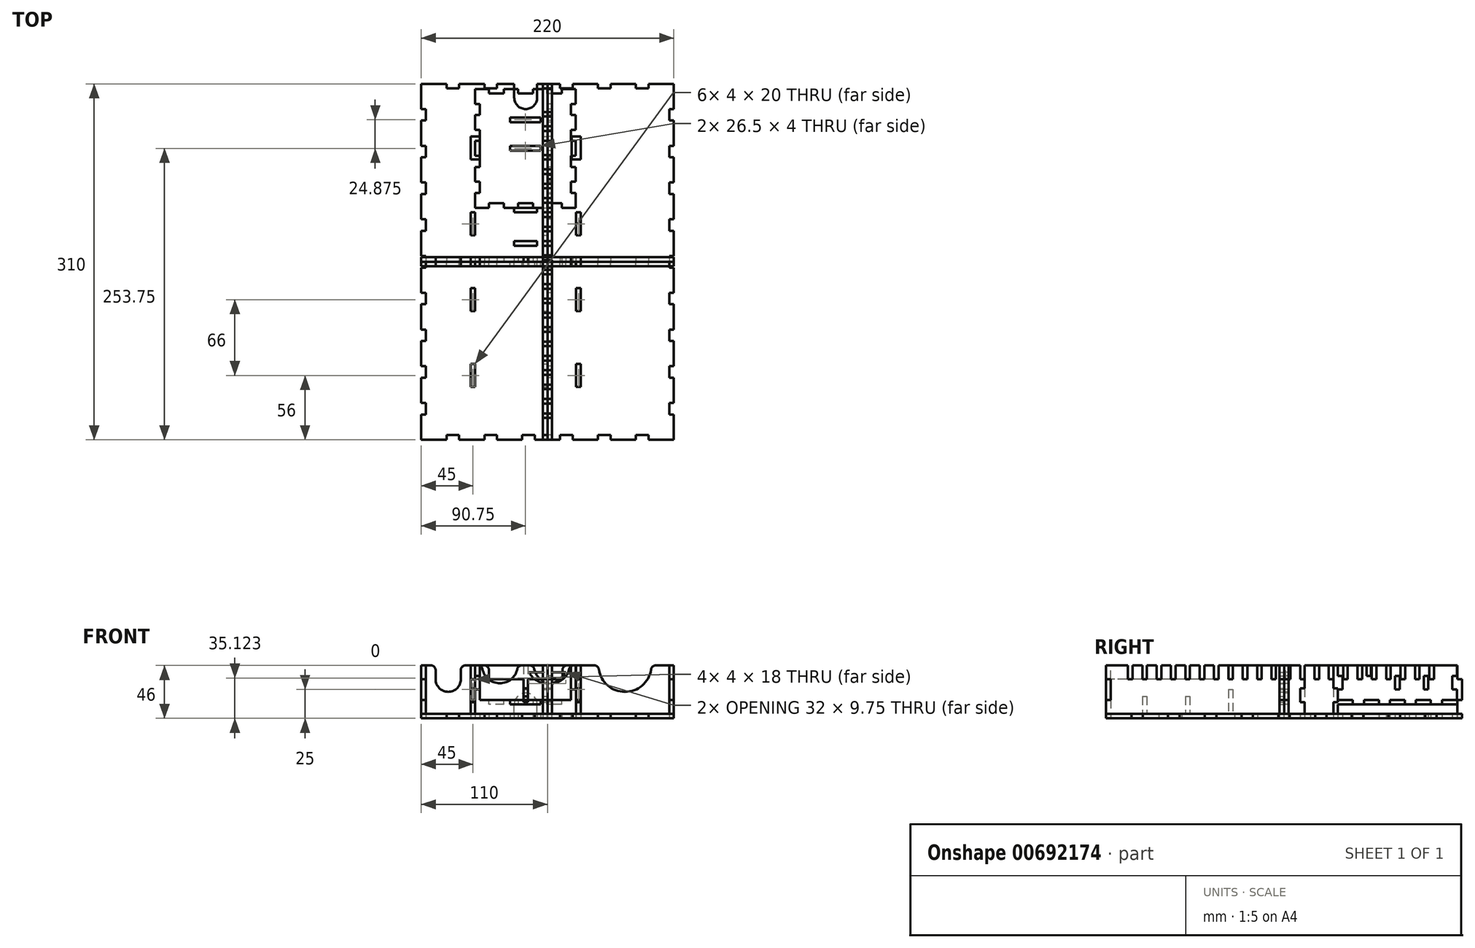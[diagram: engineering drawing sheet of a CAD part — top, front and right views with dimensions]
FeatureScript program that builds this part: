
annotation { "Feature Type Name" : "Feature", "Feature Type Description" : "" }
export const myFeature = defineFeature(function(context is Context, id is Id, definition is map)
    precondition{}
    {
        {
            assignVariable(context, id + "F0", {"name" : "thickness", "anyValue" : 4});
        }
        {
            var Q0;
            Q0=qCreatedBy(makeId("Top.planeOp"),FACE);
            var sketch = newSketch(context, id + "F1", { "sketchPlane" : qUnion([Q0])});
            skLineSegment(sketch, "E0", {"start": v(-110, 155) * mm, "end": v(-110, 133) * mm});
            skLineSegment(sketch, "E1", {"start": v(-110, 133) * mm, "end": v(-106, 133) * mm});
            skLineSegment(sketch, "E2", {"start": v(-106, 133) * mm, "end": v(-106, 123) * mm});
            skLineSegment(sketch, "E3", {"start": v(-106, 123) * mm, "end": v(-110, 123) * mm});
            skLineSegment(sketch, "E4.0.1.0", {"start": v(-106, 91) * mm, "end": v(-110, 91) * mm});
            skLineSegment(sketch, "E4.0.1.1", {"start": v(-110, 123) * mm, "end": v(-110, 101) * mm});
            skLineSegment(sketch, "E4.0.1.2", {"start": v(-106, 101) * mm, "end": v(-106, 91) * mm});
            skLineSegment(sketch, "E4.0.1.3", {"start": v(-110, 101) * mm, "end": v(-106, 101) * mm});
            skLineSegment(sketch, "E4.0.2.0", {"start": v(-106, 59) * mm, "end": v(-110, 59) * mm});
            skLineSegment(sketch, "E4.0.2.1", {"start": v(-110, 91) * mm, "end": v(-110, 69) * mm});
            skLineSegment(sketch, "E4.0.2.2", {"start": v(-106, 69) * mm, "end": v(-106, 59) * mm});
            skLineSegment(sketch, "E4.0.2.3", {"start": v(-110, 69) * mm, "end": v(-106, 69) * mm});
            skLineSegment(sketch, "E4.0.3.0", {"start": v(-106, 27) * mm, "end": v(-110, 27) * mm});
            skLineSegment(sketch, "E4.0.3.1", {"start": v(-110, 59) * mm, "end": v(-110, 37) * mm});
            skLineSegment(sketch, "E4.0.3.2", {"start": v(-106, 37) * mm, "end": v(-106, 27) * mm});
            skLineSegment(sketch, "E4.0.3.3", {"start": v(-110, 37) * mm, "end": v(-106, 37) * mm});
            skLineSegment(sketch, "E4.0.4.0", {"start": v(-106, -5) * mm, "end": v(-110, -5) * mm});
            skLineSegment(sketch, "E4.0.4.1", {"start": v(-110, 27) * mm, "end": v(-110, 5) * mm});
            skLineSegment(sketch, "E4.0.4.2", {"start": v(-106, 5) * mm, "end": v(-106, -5) * mm});
            skLineSegment(sketch, "E4.0.4.3", {"start": v(-110, 5) * mm, "end": v(-106, 5) * mm});
            skLineSegment(sketch, "E4.0.5.0", {"start": v(-106, -37) * mm, "end": v(-110, -37) * mm});
            skLineSegment(sketch, "E4.0.5.1", {"start": v(-110, -5) * mm, "end": v(-110, -27) * mm});
            skLineSegment(sketch, "E4.0.5.2", {"start": v(-106, -27) * mm, "end": v(-106, -37) * mm});
            skLineSegment(sketch, "E4.0.5.3", {"start": v(-110, -27) * mm, "end": v(-106, -27) * mm});
            skLineSegment(sketch, "E4.0.6.0", {"start": v(-106, -69) * mm, "end": v(-110, -69) * mm});
            skLineSegment(sketch, "E4.0.6.1", {"start": v(-110, -37) * mm, "end": v(-110, -59) * mm});
            skLineSegment(sketch, "E4.0.6.2", {"start": v(-106, -59) * mm, "end": v(-106, -69) * mm});
            skLineSegment(sketch, "E4.0.6.3", {"start": v(-110, -59) * mm, "end": v(-106, -59) * mm});
            skLineSegment(sketch, "E4.0.7.0", {"start": v(-106, -101) * mm, "end": v(-110, -101) * mm});
            skLineSegment(sketch, "E4.0.7.1", {"start": v(-110, -69) * mm, "end": v(-110, -91) * mm});
            skLineSegment(sketch, "E4.0.7.2", {"start": v(-106, -91) * mm, "end": v(-106, -101) * mm});
            skLineSegment(sketch, "E4.0.7.3", {"start": v(-110, -91) * mm, "end": v(-106, -91) * mm});
            skLineSegment(sketch, "E4.0.8.0", {"start": v(-106, -133) * mm, "end": v(-110, -133) * mm});
            skLineSegment(sketch, "E4.0.8.1", {"start": v(-110, -101) * mm, "end": v(-110, -123) * mm});
            skLineSegment(sketch, "E4.0.8.2", {"start": v(-106, -123) * mm, "end": v(-106, -133) * mm});
            skLineSegment(sketch, "E4.0.8.3", {"start": v(-110, -123) * mm, "end": v(-106, -123) * mm});
            skLineSegment(sketch, "E4.0.9.1", {"start": v(-110, -133) * mm, "end": v(-110, -155) * mm});
            skLineSegment(sketch, "E5", {"start": v(-110, 155) * mm, "end": v(-88, 155) * mm});
            skLineSegment(sketch, "E6", {"start": v(-88, 155) * mm, "end": v(-88, 151) * mm});
            skLineSegment(sketch, "E7", {"start": v(-88, 151) * mm, "end": v(-77, 151) * mm});
            skLineSegment(sketch, "E8", {"start": v(-77, 151) * mm, "end": v(-77, 155) * mm});
            skLineSegment(sketch, "E9.1.0.0", {"start": v(-44, 151) * mm, "end": v(-44, 155) * mm});
            skLineSegment(sketch, "E9.1.0.1", {"start": v(-55, 151) * mm, "end": v(-44, 151) * mm});
            skLineSegment(sketch, "E9.1.0.2", {"start": v(-77, 155) * mm, "end": v(-55, 155) * mm});
            skLineSegment(sketch, "E9.1.0.3", {"start": v(-55, 155) * mm, "end": v(-55, 151) * mm});
            skLineSegment(sketch, "E9.2.0.0", {"start": v(-11, 151) * mm, "end": v(-11, 155) * mm, "construction": true});
            skLineSegment(sketch, "E9.2.0.1", {"start": v(-22, 151) * mm, "end": v(-11, 151) * mm, "construction": true});
            skLineSegment(sketch, "E9.2.0.2", {"start": v(-44, 155) * mm, "end": v(-22, 155) * mm, "construction": true});
            skLineSegment(sketch, "E9.2.0.3", {"start": v(-22, 155) * mm, "end": v(-22, 151) * mm, "construction": true});
            skLineSegment(sketch, "E9.3.0.0", {"start": v(22, 151) * mm, "end": v(22, 155) * mm});
            skLineSegment(sketch, "E9.3.0.1", {"start": v(11, 151) * mm, "end": v(22, 151) * mm});
            skLineSegment(sketch, "E9.3.0.2", {"start": v(-11, 155) * mm, "end": v(11, 155) * mm, "construction": true});
            skLineSegment(sketch, "E9.3.0.3", {"start": v(11, 155) * mm, "end": v(11, 151) * mm});
            skLineSegment(sketch, "E9.4.0.0", {"start": v(55, 151) * mm, "end": v(55, 155) * mm});
            skLineSegment(sketch, "E9.4.0.1", {"start": v(44, 151) * mm, "end": v(55, 151) * mm});
            skLineSegment(sketch, "E9.4.0.2", {"start": v(22, 155) * mm, "end": v(44, 155) * mm});
            skLineSegment(sketch, "E9.4.0.3", {"start": v(44, 155) * mm, "end": v(44, 151) * mm});
            skLineSegment(sketch, "E9.5.0.0", {"start": v(88, 151) * mm, "end": v(88, 155) * mm});
            skLineSegment(sketch, "E9.5.0.1", {"start": v(77, 151) * mm, "end": v(88, 151) * mm});
            skLineSegment(sketch, "E9.5.0.2", {"start": v(55, 155) * mm, "end": v(77, 155) * mm});
            skLineSegment(sketch, "E9.5.0.3", {"start": v(77, 155) * mm, "end": v(77, 151) * mm});
            skLineSegment(sketch, "E9.6.0.2", {"start": v(88, 155) * mm, "end": v(110, 155) * mm});
            skPoint(sketch, "E10.endSnap0", {"position": v(-106, 0) * mm});
            skLineSegment(sketch, "E11.MirrorCS", {"start": v(106, -37) * mm, "end": v(110, -37) * mm});
            skLineSegment(sketch, "E12.MirrorCS", {"start": v(106, -27) * mm, "end": v(106, -37) * mm});
            skLineSegment(sketch, "E13.MirrorCS", {"start": v(106, -5) * mm, "end": v(110, -5) * mm});
            skLineSegment(sketch, "E14.MirrorCS", {"start": v(110, -133) * mm, "end": v(110, -155) * mm});
            skLineSegment(sketch, "E15.MirrorCS", {"start": v(106, 133) * mm, "end": v(106, 123) * mm});
            skLineSegment(sketch, "E16.MirrorCS", {"start": v(110, -59) * mm, "end": v(106, -59) * mm});
            skLineSegment(sketch, "E17.MirrorCS", {"start": v(110, -123) * mm, "end": v(106, -123) * mm});
            skLineSegment(sketch, "E18.MirrorCS", {"start": v(106, -91) * mm, "end": v(106, -101) * mm});
            skLineSegment(sketch, "E19.MirrorCS", {"start": v(106, -133) * mm, "end": v(110, -133) * mm});
            skLineSegment(sketch, "E20.MirrorCS", {"start": v(110, 69) * mm, "end": v(106, 69) * mm});
            skLineSegment(sketch, "E21.MirrorCS", {"start": v(106, 27) * mm, "end": v(110, 27) * mm});
            skLineSegment(sketch, "E22.MirrorCS", {"start": v(106, -101) * mm, "end": v(110, -101) * mm});
            skLineSegment(sketch, "E23.MirrorCS", {"start": v(110, -5) * mm, "end": v(110, -27) * mm});
            skLineSegment(sketch, "E24.MirrorCS", {"start": v(106, -59) * mm, "end": v(106, -69) * mm});
            skLineSegment(sketch, "E25.MirrorCS", {"start": v(106, 37) * mm, "end": v(106, 27) * mm});
            skLineSegment(sketch, "E26.MirrorCS", {"start": v(110, 133) * mm, "end": v(106, 133) * mm});
            skLineSegment(sketch, "E27.MirrorCS", {"start": v(106, 69) * mm, "end": v(106, 59) * mm});
            skLineSegment(sketch, "E28.MirrorCS", {"start": v(106, 59) * mm, "end": v(110, 59) * mm});
            skLineSegment(sketch, "E29.MirrorCS", {"start": v(110, 37) * mm, "end": v(106, 37) * mm});
            skLineSegment(sketch, "E30.MirrorCS", {"start": v(106, -69) * mm, "end": v(110, -69) * mm});
            skLineSegment(sketch, "E31.MirrorCS", {"start": v(106, 91) * mm, "end": v(110, 91) * mm});
            skLineSegment(sketch, "E32.MirrorCS", {"start": v(106, 101) * mm, "end": v(106, 91) * mm});
            skLineSegment(sketch, "E33.MirrorCS", {"start": v(110, 27) * mm, "end": v(110, 5) * mm});
            skLineSegment(sketch, "E34.MirrorCS", {"start": v(110, 5) * mm, "end": v(106, 5) * mm});
            skLineSegment(sketch, "E35.MirrorCS", {"start": v(110, 155) * mm, "end": v(110, 133) * mm});
            skLineSegment(sketch, "E36.MirrorCS", {"start": v(110, -101) * mm, "end": v(110, -123) * mm});
            skLineSegment(sketch, "E37.MirrorCS", {"start": v(106, 123) * mm, "end": v(110, 123) * mm});
            skLineSegment(sketch, "E38.MirrorCS", {"start": v(110, -27) * mm, "end": v(106, -27) * mm});
            skLineSegment(sketch, "E39.MirrorCS", {"start": v(106, -123) * mm, "end": v(106, -133) * mm});
            skLineSegment(sketch, "E40.MirrorCS", {"start": v(110, -91) * mm, "end": v(106, -91) * mm});
            skLineSegment(sketch, "E41.MirrorCS", {"start": v(106, 5) * mm, "end": v(106, -5) * mm});
            skLineSegment(sketch, "E42.MirrorCS", {"start": v(110, 101) * mm, "end": v(106, 101) * mm});
            skLineSegment(sketch, "E43.MirrorCS", {"start": v(110, 59) * mm, "end": v(110, 37) * mm});
            skLineSegment(sketch, "E44.MirrorCS", {"start": v(110, -69) * mm, "end": v(110, -91) * mm});
            skLineSegment(sketch, "E45.MirrorCS", {"start": v(110, 91) * mm, "end": v(110, 69) * mm});
            skLineSegment(sketch, "E46.MirrorCS", {"start": v(110, -37) * mm, "end": v(110, -59) * mm});
            skLineSegment(sketch, "E47.MirrorCS", {"start": v(110, 123) * mm, "end": v(110, 101) * mm});
            skLineSegment(sketch, "E48.MirrorCS", {"start": v(-11, -151) * mm, "end": v(-11, -155) * mm});
            skLineSegment(sketch, "E49.MirrorCS", {"start": v(22, -155) * mm, "end": v(44, -155) * mm});
            skLineSegment(sketch, "E50.MirrorCS", {"start": v(-55, -151) * mm, "end": v(-44, -151) * mm});
            skLineSegment(sketch, "E51.MirrorCS", {"start": v(-44, -151) * mm, "end": v(-44, -155) * mm});
            skLineSegment(sketch, "E52.MirrorCS", {"start": v(11, -151) * mm, "end": v(22, -151) * mm});
            skLineSegment(sketch, "E53.MirrorCS", {"start": v(22, -151) * mm, "end": v(22, -155) * mm});
            skLineSegment(sketch, "E54.MirrorCS", {"start": v(-22, -151) * mm, "end": v(-11, -151) * mm});
            skLineSegment(sketch, "E55.MirrorCS", {"start": v(77, -151) * mm, "end": v(88, -151) * mm});
            skLineSegment(sketch, "E56.MirrorCS", {"start": v(-11, -155) * mm, "end": v(11, -155) * mm});
            skLineSegment(sketch, "E57.MirrorCS", {"start": v(-77, -155) * mm, "end": v(-55, -155) * mm});
            skLineSegment(sketch, "E58.MirrorCS", {"start": v(-88, -155) * mm, "end": v(-88, -151) * mm});
            skLineSegment(sketch, "E59.MirrorCS", {"start": v(-22, -155) * mm, "end": v(-22, -151) * mm});
            skLineSegment(sketch, "E60.MirrorCS", {"start": v(44, -155) * mm, "end": v(44, -151) * mm});
            skLineSegment(sketch, "E61.MirrorCS", {"start": v(44, -151) * mm, "end": v(55, -151) * mm});
            skLineSegment(sketch, "E62.MirrorCS", {"start": v(-77, -151) * mm, "end": v(-77, -155) * mm});
            skLineSegment(sketch, "E63.MirrorCS", {"start": v(77, -155) * mm, "end": v(77, -151) * mm});
            skLineSegment(sketch, "E64.MirrorCS", {"start": v(88, -155) * mm, "end": v(110, -155) * mm});
            skLineSegment(sketch, "E65.MirrorCS", {"start": v(-110, -155) * mm, "end": v(-88, -155) * mm});
            skLineSegment(sketch, "E66.MirrorCS", {"start": v(11, -155) * mm, "end": v(11, -151) * mm});
            skLineSegment(sketch, "E67.MirrorCS", {"start": v(-55, -155) * mm, "end": v(-55, -151) * mm});
            skLineSegment(sketch, "E68.MirrorCS", {"start": v(55, -151) * mm, "end": v(55, -155) * mm});
            skLineSegment(sketch, "E69.MirrorCS", {"start": v(88, -151) * mm, "end": v(88, -155) * mm});
            skLineSegment(sketch, "E70.MirrorCS", {"start": v(-88, -151) * mm, "end": v(-77, -151) * mm});
            skLineSegment(sketch, "E71.MirrorCS", {"start": v(55, -155) * mm, "end": v(77, -155) * mm});
            skLineSegment(sketch, "E72.MirrorCS", {"start": v(-44, -155) * mm, "end": v(-22, -155) * mm});
            skLineSegment(sketch, "E73", {"start": v(-65, 163.65) * mm, "end": v(-65, -222.9) * mm, "construction": true});
            skLineSegment(sketch, "E74", {"start": v(-19, 166.4) * mm, "end": v(-19, -214.65) * mm, "construction": true});
            skLineSegment(sketch, "E75", {"start": v(27, 161.08) * mm, "end": v(27, -222.02) * mm, "construction": true});
            skLineSegment(sketch, "E76", {"start": v(-29, 155) * mm, "end": v(-29, 143) * mm});
            skLineSegment(sketch, "E77", {"start": v(-9, 155) * mm, "end": v(-9, 143) * mm});
            skArc(sketch, "E78", {"start": v(-29, 143) * mm, "mid": v(-19, 133) * mm, "end": v(-9, 143) * mm});
            skLineSegment(sketch, "E79", {"start": v(-44, 155) * mm, "end": v(-29, 155) * mm});
            skLineSegment(sketch, "E80", {"start": v(-9, 155) * mm, "end": v(11, 155) * mm});
            skLineSegment(sketch, "E81.bottom", {"start": v(21, 109) * mm, "end": v(29, 109) * mm});
            skLineSegment(sketch, "E81.top", {"start": v(21, 89) * mm, "end": v(29, 89) * mm});
            skLineSegment(sketch, "E81.left", {"start": v(21, 109) * mm, "end": v(21, 89) * mm});
            skLineSegment(sketch, "E81.right", {"start": v(29, 109) * mm, "end": v(29, 89) * mm});
            skLineSegment(sketch, "E82.bottom", {"start": v(25, 43) * mm, "end": v(29, 43) * mm});
            skLineSegment(sketch, "E82.top", {"start": v(25, 23) * mm, "end": v(29, 23) * mm});
            skLineSegment(sketch, "E82.left", {"start": v(25, 43) * mm, "end": v(25, 23) * mm});
            skLineSegment(sketch, "E82.right", {"start": v(29, 43) * mm, "end": v(29, 23) * mm});
            skLineSegment(sketch, "E83.bottom", {"start": v(25, -23) * mm, "end": v(29, -23) * mm});
            skLineSegment(sketch, "E83.top", {"start": v(25, -43) * mm, "end": v(29, -43) * mm});
            skLineSegment(sketch, "E83.left", {"start": v(25, -23) * mm, "end": v(25, -43) * mm});
            skLineSegment(sketch, "E83.right", {"start": v(29, -23) * mm, "end": v(29, -43) * mm});
            skLineSegment(sketch, "E84.bottom", {"start": v(25, -89) * mm, "end": v(29, -89) * mm});
            skLineSegment(sketch, "E84.top", {"start": v(25, -109) * mm, "end": v(29, -109) * mm});
            skLineSegment(sketch, "E84.left", {"start": v(25, -89) * mm, "end": v(25, -109) * mm});
            skLineSegment(sketch, "E84.right", {"start": v(29, -89) * mm, "end": v(29, -109) * mm});
            skLineSegment(sketch, "E85", {"start": v(29, 109) * mm, "end": v(29, 155) * mm, "construction": true});
            skPoint(sketch, "E85.endSnap0", {"position": v(33, 155) * mm});
            skLineSegment(sketch, "E86", {"start": v(29, 89) * mm, "end": v(29, 43) * mm, "construction": true});
            skLineSegment(sketch, "E87", {"start": v(29, 23) * mm, "end": v(29, -23) * mm, "construction": true});
            skLineSegment(sketch, "E88", {"start": v(29, -43) * mm, "end": v(29, -89) * mm, "construction": true});
            skLineSegment(sketch, "E89", {"start": v(29, -109) * mm, "end": v(29, -155) * mm, "construction": true});
            skLineSegment(sketch, "E90.MirrorCS", {"start": v(-63, -109) * mm, "end": v(-67, -109) * mm});
            skLineSegment(sketch, "E91.MirrorCS", {"start": v(-59, 109) * mm, "end": v(-67, 109) * mm});
            skLineSegment(sketch, "E92.MirrorCS", {"start": v(-63, 43) * mm, "end": v(-67, 43) * mm});
            skLineSegment(sketch, "E93.MirrorCS", {"start": v(-59, 89) * mm, "end": v(-67, 89) * mm});
            skLineSegment(sketch, "E94.MirrorCS", {"start": v(-63, -23) * mm, "end": v(-67, -23) * mm});
            skLineSegment(sketch, "E95.MirrorCS", {"start": v(-63, 23) * mm, "end": v(-67, 23) * mm});
            skLineSegment(sketch, "E96.MirrorCS", {"start": v(-63, -89) * mm, "end": v(-67, -89) * mm});
            skLineSegment(sketch, "E97.MirrorCS", {"start": v(-63, -43) * mm, "end": v(-67, -43) * mm});
            skLineSegment(sketch, "E98.MirrorCS", {"start": v(-67, -89) * mm, "end": v(-67, -109) * mm});
            skLineSegment(sketch, "E99.MirrorCS", {"start": v(-67, -23) * mm, "end": v(-67, -43) * mm});
            skLineSegment(sketch, "E100.MirrorCS", {"start": v(-59, 109) * mm, "end": v(-59, 89) * mm});
            skLineSegment(sketch, "E101.MirrorCS", {"start": v(-63, 43) * mm, "end": v(-63, 23) * mm});
            skLineSegment(sketch, "E102.MirrorCS", {"start": v(-67, 109) * mm, "end": v(-67, 89) * mm});
            skLineSegment(sketch, "E103.MirrorCS", {"start": v(-67, 43) * mm, "end": v(-67, 23) * mm});
            skLineSegment(sketch, "E104.MirrorCS", {"start": v(-63, -89) * mm, "end": v(-63, -109) * mm});
            skLineSegment(sketch, "E105.MirrorCS", {"start": v(-63, -23) * mm, "end": v(-63, -43) * mm});
            skLineSegment(sketch, "E106", {"start": v(-151.25, 45) * mm, "end": v(136.26, 45) * mm, "construction": true});
            skLineSegment(sketch, "E107", {"start": v(137.08, 16) * mm, "end": v(-152.07, 16) * mm, "construction": true});
            skLineSegment(sketch, "E108.bottom", {"start": v(-29, 47) * mm, "end": v(-9, 47) * mm});
            skLineSegment(sketch, "E108.top", {"start": v(-29, 43) * mm, "end": v(-9, 43) * mm});
            skLineSegment(sketch, "E108.left", {"start": v(-29, 47) * mm, "end": v(-29, 43) * mm});
            skLineSegment(sketch, "E108.right", {"start": v(-9, 47) * mm, "end": v(-9, 43) * mm});
            skLineSegment(sketch, "E109.bottom", {"start": v(-29, 18) * mm, "end": v(-9, 18) * mm});
            skLineSegment(sketch, "E109.top", {"start": v(-29, 14) * mm, "end": v(-9, 14) * mm});
            skLineSegment(sketch, "E109.left", {"start": v(-29, 18) * mm, "end": v(-29, 14) * mm});
            skLineSegment(sketch, "E109.right", {"start": v(-9, 18) * mm, "end": v(-9, 14) * mm});
            skSolve(sketch);
        }
        {
            var Q0;
            Q0=qSketchRegion(id+"F1",true);
            extrude(context, id + "F2", {"entities" : qUnion([Q0]), "depth" : 4 * mm});
        }
        {
            var Q0;
            Q0=qCreatedBy(makeId("Right.planeOp"),FACE);
            var sketch = newSketch(context, id + "F3", { "sketchPlane" : qUnion([Q0])});
            skLineSegment(sketch, "E110.top", {"start": v(-151, 4) * mm, "end": v(151, 4) * mm});
            skLineSegment(sketch, "E111.bottom", {"start": v(-151, 34) * mm, "end": v(-155, 34) * mm});
            skLineSegment(sketch, "E111.top", {"start": v(-151, 16) * mm, "end": v(-155, 16) * mm});
            skPoint(sketch, "E112.oppositeSnap0", {"position": v(-153, 16) * mm});
            skLineSegment(sketch, "E112.bottom", {"start": v(155, 34) * mm, "end": v(151, 34) * mm});
            skLineSegment(sketch, "E112.top", {"start": v(155, 16) * mm, "end": v(151, 16) * mm});
            skLineSegment(sketch, "E113.bottom", {"start": v(-133, 0) * mm, "end": v(-123, 0) * mm});
            skLineSegment(sketch, "E113.top", {"start": v(-133, 4) * mm, "end": v(-123, 4) * mm});
            skLineSegment(sketch, "E113.left", {"start": v(-133, 0) * mm, "end": v(-133, 4) * mm});
            skLineSegment(sketch, "E113.right", {"start": v(-123, 0) * mm, "end": v(-123, 4) * mm});
            skLineSegment(sketch, "E114.1.0.0", {"start": v(-101, 4) * mm, "end": v(-91, 4) * mm});
            skLineSegment(sketch, "E114.1.0.1", {"start": v(-101, 0) * mm, "end": v(-101, 4) * mm});
            skLineSegment(sketch, "E114.1.0.2", {"start": v(-91, 0) * mm, "end": v(-91, 4) * mm});
            skLineSegment(sketch, "E114.1.0.3", {"start": v(-101, 0) * mm, "end": v(-91, 0) * mm});
            skLineSegment(sketch, "E114.2.0.0", {"start": v(-69, 4) * mm, "end": v(-59, 4) * mm});
            skLineSegment(sketch, "E114.2.0.1", {"start": v(-69, 0) * mm, "end": v(-69, 4) * mm});
            skLineSegment(sketch, "E114.2.0.2", {"start": v(-59, 0) * mm, "end": v(-59, 4) * mm});
            skLineSegment(sketch, "E114.2.0.3", {"start": v(-69, 0) * mm, "end": v(-59, 0) * mm});
            skLineSegment(sketch, "E114.3.0.0", {"start": v(-37, 4) * mm, "end": v(-27, 4) * mm});
            skLineSegment(sketch, "E114.3.0.1", {"start": v(-37, 0) * mm, "end": v(-37, 4) * mm});
            skLineSegment(sketch, "E114.3.0.2", {"start": v(-27, 0) * mm, "end": v(-27, 4) * mm});
            skLineSegment(sketch, "E114.3.0.3", {"start": v(-37, 0) * mm, "end": v(-27, 0) * mm});
            skLineSegment(sketch, "E114.4.0.0", {"start": v(-5, 4) * mm, "end": v(5, 4) * mm});
            skLineSegment(sketch, "E114.4.0.1", {"start": v(-5, 0) * mm, "end": v(-5, 4) * mm});
            skLineSegment(sketch, "E114.4.0.2", {"start": v(5, 0) * mm, "end": v(5, 4) * mm});
            skLineSegment(sketch, "E114.4.0.3", {"start": v(-5, 0) * mm, "end": v(5, 0) * mm});
            skLineSegment(sketch, "E114.5.0.0", {"start": v(27, 4) * mm, "end": v(37, 4) * mm});
            skLineSegment(sketch, "E114.5.0.1", {"start": v(27, 0) * mm, "end": v(27, 4) * mm});
            skLineSegment(sketch, "E114.5.0.2", {"start": v(37, 0) * mm, "end": v(37, 4) * mm});
            skLineSegment(sketch, "E114.5.0.3", {"start": v(27, 0) * mm, "end": v(37, 0) * mm});
            skLineSegment(sketch, "E114.6.0.0", {"start": v(59, 4) * mm, "end": v(69, 4) * mm});
            skLineSegment(sketch, "E114.6.0.1", {"start": v(59, 0) * mm, "end": v(59, 4) * mm});
            skLineSegment(sketch, "E114.6.0.2", {"start": v(69, 0) * mm, "end": v(69, 4) * mm});
            skLineSegment(sketch, "E114.6.0.3", {"start": v(59, 0) * mm, "end": v(69, 0) * mm});
            skLineSegment(sketch, "E114.7.0.0", {"start": v(91, 4) * mm, "end": v(101, 4) * mm});
            skLineSegment(sketch, "E114.7.0.1", {"start": v(91, 0) * mm, "end": v(91, 4) * mm});
            skLineSegment(sketch, "E114.7.0.2", {"start": v(101, 0) * mm, "end": v(101, 4) * mm});
            skLineSegment(sketch, "E114.7.0.3", {"start": v(91, 0) * mm, "end": v(101, 0) * mm});
            skLineSegment(sketch, "E114.8.0.0", {"start": v(123, 4) * mm, "end": v(133, 4) * mm});
            skLineSegment(sketch, "E114.8.0.1", {"start": v(123, 0) * mm, "end": v(123, 4) * mm});
            skLineSegment(sketch, "E114.8.0.2", {"start": v(133, 0) * mm, "end": v(133, 4) * mm});
            skLineSegment(sketch, "E114.8.0.3", {"start": v(123, 0) * mm, "end": v(133, 0) * mm});
            skLineSegment(sketch, "E114.direction1", {"start": v(-133, 0) * mm, "end": v(-101, 0) * mm, "construction": true});
            skLineSegment(sketch, "E115.top", {"start": v(-151, 46) * mm, "end": v(-136, 46) * mm});
            skLineSegment(sketch, "E115.right", {"start": v(-136, 34) * mm, "end": v(-136, 46) * mm});
            skLineSegment(sketch, "E116.top", {"start": v(151, 46) * mm, "end": v(130.5, 46) * mm});
            skLineSegment(sketch, "E116.right", {"start": v(130.5, 34) * mm, "end": v(130.5, 46) * mm});
            skLineSegment(sketch, "E117.top", {"start": v(-132, 46) * mm, "end": v(-123.5, 46) * mm});
            skLineSegment(sketch, "E117.left", {"start": v(-132, 34) * mm, "end": v(-132, 46) * mm});
            skLineSegment(sketch, "E117.right", {"start": v(-123.5, 34) * mm, "end": v(-123.5, 46) * mm});
            skLineSegment(sketch, "E118", {"start": v(-136, 34) * mm, "end": v(-132, 34) * mm});
            skLineSegment(sketch, "E119", {"start": v(130.5, 34) * mm, "end": v(126.5, 34) * mm});
            skLineSegment(sketch, "E120.1.0.0", {"start": v(-123.5, 34) * mm, "end": v(-119.5, 34) * mm});
            skLineSegment(sketch, "E120.1.0.1", {"start": v(-111, 34) * mm, "end": v(-111, 46) * mm});
            skLineSegment(sketch, "E120.1.0.2", {"start": v(-119.5, 46) * mm, "end": v(-111, 46) * mm});
            skLineSegment(sketch, "E120.1.0.3", {"start": v(-119.5, 34) * mm, "end": v(-119.5, 46) * mm});
            skLineSegment(sketch, "E120.2.0.0", {"start": v(-111, 34) * mm, "end": v(-107, 34) * mm});
            skLineSegment(sketch, "E120.2.0.1", {"start": v(-98.5, 34) * mm, "end": v(-98.5, 46) * mm});
            skLineSegment(sketch, "E120.2.0.2", {"start": v(-107, 46) * mm, "end": v(-98.5, 46) * mm});
            skLineSegment(sketch, "E120.2.0.3", {"start": v(-107, 34) * mm, "end": v(-107, 46) * mm});
            skLineSegment(sketch, "E120.3.0.0", {"start": v(-98.5, 34) * mm, "end": v(-94.5, 34) * mm});
            skLineSegment(sketch, "E120.3.0.1", {"start": v(-86, 34) * mm, "end": v(-86, 46) * mm});
            skLineSegment(sketch, "E120.3.0.2", {"start": v(-94.5, 46) * mm, "end": v(-86, 46) * mm});
            skLineSegment(sketch, "E120.3.0.3", {"start": v(-94.5, 34) * mm, "end": v(-94.5, 46) * mm});
            skLineSegment(sketch, "E120.4.0.0", {"start": v(-86, 34) * mm, "end": v(-82, 34) * mm});
            skLineSegment(sketch, "E120.4.0.1", {"start": v(-73.5, 34) * mm, "end": v(-73.5, 46) * mm});
            skLineSegment(sketch, "E120.4.0.2", {"start": v(-82, 46) * mm, "end": v(-73.5, 46) * mm});
            skLineSegment(sketch, "E120.4.0.3", {"start": v(-82, 34) * mm, "end": v(-82, 46) * mm});
            skLineSegment(sketch, "E120.5.0.0", {"start": v(-73.5, 34) * mm, "end": v(-69.5, 34) * mm});
            skLineSegment(sketch, "E120.5.0.1", {"start": v(-61, 34) * mm, "end": v(-61, 46) * mm});
            skLineSegment(sketch, "E120.5.0.2", {"start": v(-69.5, 46) * mm, "end": v(-61, 46) * mm});
            skLineSegment(sketch, "E120.5.0.3", {"start": v(-69.5, 34) * mm, "end": v(-69.5, 46) * mm});
            skLineSegment(sketch, "E120.6.0.0", {"start": v(-61, 34) * mm, "end": v(-57, 34) * mm});
            skLineSegment(sketch, "E120.6.0.1", {"start": v(-48.5, 34) * mm, "end": v(-48.5, 46) * mm});
            skLineSegment(sketch, "E120.6.0.2", {"start": v(-57, 46) * mm, "end": v(-48.5, 46) * mm});
            skLineSegment(sketch, "E120.6.0.3", {"start": v(-57, 34) * mm, "end": v(-57, 46) * mm});
            skLineSegment(sketch, "E120.7.0.0", {"start": v(-48.5, 34) * mm, "end": v(-44.5, 34) * mm});
            skLineSegment(sketch, "E120.7.0.1", {"start": v(-36, 34) * mm, "end": v(-36, 46) * mm});
            skLineSegment(sketch, "E120.7.0.2", {"start": v(-44.5, 46) * mm, "end": v(-36, 46) * mm});
            skLineSegment(sketch, "E120.7.0.3", {"start": v(-44.5, 34) * mm, "end": v(-44.5, 46) * mm});
            skLineSegment(sketch, "E120.8.0.0", {"start": v(-36, 34) * mm, "end": v(-32, 34) * mm});
            skLineSegment(sketch, "E120.8.0.1", {"start": v(-23.5, 34) * mm, "end": v(-23.5, 46) * mm});
            skLineSegment(sketch, "E120.8.0.2", {"start": v(-32, 46) * mm, "end": v(-23.5, 46) * mm});
            skLineSegment(sketch, "E120.8.0.3", {"start": v(-32, 34) * mm, "end": v(-32, 46) * mm});
            skLineSegment(sketch, "E120.9.0.0", {"start": v(-23.5, 34) * mm, "end": v(-19.5, 34) * mm});
            skLineSegment(sketch, "E120.9.0.1", {"start": v(-11, 34) * mm, "end": v(-11, 46) * mm});
            skLineSegment(sketch, "E120.9.0.2", {"start": v(-19.5, 46) * mm, "end": v(-11, 46) * mm});
            skLineSegment(sketch, "E120.9.0.3", {"start": v(-19.5, 34) * mm, "end": v(-19.5, 46) * mm});
            skLineSegment(sketch, "E120.10.0.0", {"start": v(-11, 34) * mm, "end": v(-7, 34) * mm});
            skLineSegment(sketch, "E120.10.0.1", {"start": v(1.5, 34) * mm, "end": v(1.5, 46) * mm});
            skLineSegment(sketch, "E120.10.0.2", {"start": v(-7, 46) * mm, "end": v(1.5, 46) * mm});
            skLineSegment(sketch, "E120.10.0.3", {"start": v(-7, 34) * mm, "end": v(-7, 46) * mm});
            skLineSegment(sketch, "E120.11.0.0", {"start": v(1.5, 34) * mm, "end": v(5.5, 34) * mm});
            skLineSegment(sketch, "E120.11.0.1", {"start": v(14, 34) * mm, "end": v(14, 46) * mm});
            skLineSegment(sketch, "E120.11.0.2", {"start": v(5.5, 46) * mm, "end": v(14, 46) * mm});
            skLineSegment(sketch, "E120.11.0.3", {"start": v(5.5, 34) * mm, "end": v(5.5, 46) * mm});
            skLineSegment(sketch, "E120.12.0.0", {"start": v(14, 34) * mm, "end": v(18, 34) * mm});
            skLineSegment(sketch, "E120.12.0.1", {"start": v(26.5, 34) * mm, "end": v(26.5, 46) * mm});
            skLineSegment(sketch, "E120.12.0.2", {"start": v(18, 46) * mm, "end": v(26.5, 46) * mm});
            skLineSegment(sketch, "E120.12.0.3", {"start": v(18, 34) * mm, "end": v(18, 46) * mm});
            skLineSegment(sketch, "E120.13.0.0", {"start": v(26.5, 34) * mm, "end": v(30.5, 34) * mm});
            skLineSegment(sketch, "E120.13.0.1", {"start": v(39, 34) * mm, "end": v(39, 46) * mm});
            skLineSegment(sketch, "E120.13.0.2", {"start": v(30.5, 46) * mm, "end": v(39, 46) * mm});
            skLineSegment(sketch, "E120.13.0.3", {"start": v(30.5, 34) * mm, "end": v(30.5, 46) * mm});
            skLineSegment(sketch, "E120.14.0.0", {"start": v(39, 34) * mm, "end": v(43, 34) * mm});
            skLineSegment(sketch, "E120.14.0.1", {"start": v(51.5, 34) * mm, "end": v(51.5, 46) * mm});
            skLineSegment(sketch, "E120.14.0.2", {"start": v(43, 46) * mm, "end": v(51.5, 46) * mm});
            skLineSegment(sketch, "E120.14.0.3", {"start": v(43, 34) * mm, "end": v(43, 46) * mm});
            skLineSegment(sketch, "E120.15.0.0", {"start": v(51.5, 34) * mm, "end": v(55.5, 34) * mm});
            skLineSegment(sketch, "E120.15.0.1", {"start": v(64, 34) * mm, "end": v(64, 46) * mm});
            skLineSegment(sketch, "E120.15.0.2", {"start": v(55.5, 46) * mm, "end": v(64, 46) * mm});
            skLineSegment(sketch, "E120.15.0.3", {"start": v(55.5, 34) * mm, "end": v(55.5, 46) * mm});
            skLineSegment(sketch, "E120.16.0.0", {"start": v(64, 34) * mm, "end": v(68, 34) * mm});
            skLineSegment(sketch, "E120.16.0.1", {"start": v(76.5, 34) * mm, "end": v(76.5, 46) * mm});
            skLineSegment(sketch, "E120.16.0.2", {"start": v(68, 46) * mm, "end": v(76.5, 46) * mm});
            skLineSegment(sketch, "E120.16.0.3", {"start": v(68, 34) * mm, "end": v(68, 46) * mm});
            skLineSegment(sketch, "E120.17.0.0", {"start": v(76.5, 34) * mm, "end": v(80.5, 34) * mm});
            skLineSegment(sketch, "E120.17.0.1", {"start": v(89, 34) * mm, "end": v(89, 46) * mm});
            skLineSegment(sketch, "E120.17.0.2", {"start": v(80.5, 46) * mm, "end": v(89, 46) * mm});
            skLineSegment(sketch, "E120.17.0.3", {"start": v(80.5, 34) * mm, "end": v(80.5, 46) * mm});
            skLineSegment(sketch, "E120.18.0.0", {"start": v(89, 34) * mm, "end": v(93, 34) * mm});
            skLineSegment(sketch, "E120.18.0.1", {"start": v(101.5, 34) * mm, "end": v(101.5, 46) * mm});
            skLineSegment(sketch, "E120.18.0.2", {"start": v(93, 46) * mm, "end": v(101.5, 46) * mm});
            skLineSegment(sketch, "E120.18.0.3", {"start": v(93, 34) * mm, "end": v(93, 46) * mm});
            skLineSegment(sketch, "E120.19.0.0", {"start": v(101.5, 34) * mm, "end": v(105.5, 34) * mm});
            skLineSegment(sketch, "E120.19.0.1", {"start": v(114, 34) * mm, "end": v(114, 46) * mm});
            skLineSegment(sketch, "E120.19.0.2", {"start": v(105.5, 46) * mm, "end": v(114, 46) * mm});
            skLineSegment(sketch, "E120.19.0.3", {"start": v(105.5, 34) * mm, "end": v(105.5, 46) * mm});
            skLineSegment(sketch, "E120.20.0.0", {"start": v(114, 34) * mm, "end": v(118, 34) * mm});
            skLineSegment(sketch, "E120.20.0.1", {"start": v(126.5, 34) * mm, "end": v(126.5, 46) * mm});
            skLineSegment(sketch, "E120.20.0.2", {"start": v(118, 46) * mm, "end": v(126.5, 46) * mm});
            skLineSegment(sketch, "E120.20.0.3", {"start": v(118, 34) * mm, "end": v(118, 46) * mm});
            skLineSegment(sketch, "E121", {"start": v(18, 84.68) * mm, "end": v(18, -61.22) * mm, "construction": true});
            skLineSegment(sketch, "E122", {"start": v(43, 84.72) * mm, "end": v(43, -60.85) * mm, "construction": true});
            skLineSegment(sketch, "E123", {"start": v(155, 34) * mm, "end": v(155, 16) * mm});
            skLineSegment(sketch, "E124", {"start": v(151, 34) * mm, "end": v(151, 46) * mm});
            skLineSegment(sketch, "E125", {"start": v(151, 16) * mm, "end": v(151, 4) * mm});
            skLineSegment(sketch, "E126", {"start": v(-151, 46) * mm, "end": v(-155, 46) * mm});
            skLineSegment(sketch, "E127", {"start": v(-155, 46) * mm, "end": v(-155, 34) * mm});
            skLineSegment(sketch, "E128", {"start": v(-155, 16) * mm, "end": v(-155, 4) * mm});
            skLineSegment(sketch, "E129", {"start": v(-155, 4) * mm, "end": v(-151, 4) * mm});
            skLineSegment(sketch, "E130", {"start": v(-151, 34) * mm, "end": v(-151, 16) * mm});
            skLineSegment(sketch, "E131", {"start": v(47, -59.92) * mm, "end": v(47, 83.22) * mm, "construction": true});
            skLineSegment(sketch, "E132", {"start": v(14, 85.2) * mm, "end": v(14, -60.46) * mm, "construction": true});
            skSolve(sketch);
        }
        {
            var Q0;
            Q0=qSketchRegion(id+"F3",true);
            extrude(context, id + "F4", {"entities" : qUnion([Q0]), "depth" : 4 * mm});
        }
        {
            var Q0;
            Q0=qCreatedBy(makeId("Right.planeOp"),FACE);
            var sketch = newSketch(context, id + "F5", { "sketchPlane" : qUnion([Q0])});
            skLineSegment(sketch, "E133.bottom", {"start": v(-151, 34) * mm, "end": v(-155, 34) * mm});
            skLineSegment(sketch, "E133.top", {"start": v(-151, 16) * mm, "end": v(-155, 16) * mm});
            skLineSegment(sketch, "E133.right", {"start": v(-155, 34) * mm, "end": v(-155, 16) * mm});
            skPoint(sketch, "E134.oppositeSnap0", {"position": v(-153, 16) * mm});
            skLineSegment(sketch, "E134.right", {"start": v(155, 34) * mm, "end": v(155, 16) * mm});
            skLineSegment(sketch, "E135", {"start": v(-151, 16) * mm, "end": v(-151, 4) * mm});
            skLineSegment(sketch, "E136.right", {"start": v(-136, 34) * mm, "end": v(-136, 46) * mm});
            skLineSegment(sketch, "E137.right", {"start": v(130.5, 34) * mm, "end": v(130.5, 46) * mm});
            skLineSegment(sketch, "E138.top", {"start": v(-132, 46) * mm, "end": v(-123.5, 46) * mm});
            skLineSegment(sketch, "E138.left", {"start": v(-132, 34) * mm, "end": v(-132, 46) * mm});
            skLineSegment(sketch, "E138.right", {"start": v(-123.5, 34) * mm, "end": v(-123.5, 46) * mm});
            skLineSegment(sketch, "E139", {"start": v(-136, 34) * mm, "end": v(-132, 34) * mm});
            skLineSegment(sketch, "E140", {"start": v(130.5, 34) * mm, "end": v(126.5, 34) * mm});
            skLineSegment(sketch, "E141.1.0.0", {"start": v(-123.5, 34) * mm, "end": v(-119.5, 34) * mm});
            skLineSegment(sketch, "E141.1.0.1", {"start": v(-111, 34) * mm, "end": v(-111, 46) * mm});
            skLineSegment(sketch, "E141.1.0.2", {"start": v(-119.5, 46) * mm, "end": v(-111, 46) * mm});
            skLineSegment(sketch, "E141.1.0.3", {"start": v(-119.5, 34) * mm, "end": v(-119.5, 46) * mm});
            skLineSegment(sketch, "E141.2.0.0", {"start": v(-111, 34) * mm, "end": v(-107, 34) * mm});
            skLineSegment(sketch, "E141.2.0.1", {"start": v(-98.5, 34) * mm, "end": v(-98.5, 46) * mm});
            skLineSegment(sketch, "E141.2.0.2", {"start": v(-107, 46) * mm, "end": v(-98.5, 46) * mm});
            skLineSegment(sketch, "E141.2.0.3", {"start": v(-107, 34) * mm, "end": v(-107, 46) * mm});
            skLineSegment(sketch, "E141.3.0.0", {"start": v(-98.5, 34) * mm, "end": v(-94.5, 34) * mm});
            skLineSegment(sketch, "E141.3.0.1", {"start": v(-86, 34) * mm, "end": v(-86, 46) * mm});
            skLineSegment(sketch, "E141.3.0.2", {"start": v(-94.5, 46) * mm, "end": v(-86, 46) * mm});
            skLineSegment(sketch, "E141.3.0.3", {"start": v(-94.5, 34) * mm, "end": v(-94.5, 46) * mm});
            skLineSegment(sketch, "E141.4.0.0", {"start": v(-86, 34) * mm, "end": v(-82, 34) * mm});
            skLineSegment(sketch, "E141.4.0.1", {"start": v(-73.5, 34) * mm, "end": v(-73.5, 46) * mm});
            skLineSegment(sketch, "E141.4.0.2", {"start": v(-82, 46) * mm, "end": v(-73.5, 46) * mm});
            skLineSegment(sketch, "E141.4.0.3", {"start": v(-82, 34) * mm, "end": v(-82, 46) * mm});
            skLineSegment(sketch, "E141.5.0.0", {"start": v(-73.5, 34) * mm, "end": v(-69.5, 34) * mm});
            skLineSegment(sketch, "E141.5.0.1", {"start": v(-61, 34) * mm, "end": v(-61, 46) * mm});
            skLineSegment(sketch, "E141.5.0.2", {"start": v(-69.5, 46) * mm, "end": v(-61, 46) * mm});
            skLineSegment(sketch, "E141.5.0.3", {"start": v(-69.5, 34) * mm, "end": v(-69.5, 46) * mm});
            skLineSegment(sketch, "E141.6.0.0", {"start": v(-61, 34) * mm, "end": v(-57, 34) * mm});
            skLineSegment(sketch, "E141.6.0.1", {"start": v(-48.5, 34) * mm, "end": v(-48.5, 46) * mm});
            skLineSegment(sketch, "E141.6.0.2", {"start": v(-57, 46) * mm, "end": v(-48.5, 46) * mm});
            skLineSegment(sketch, "E141.6.0.3", {"start": v(-57, 34) * mm, "end": v(-57, 46) * mm});
            skLineSegment(sketch, "E141.7.0.0", {"start": v(-48.5, 34) * mm, "end": v(-44.5, 34) * mm});
            skLineSegment(sketch, "E141.7.0.1", {"start": v(-36, 34) * mm, "end": v(-36, 46) * mm});
            skLineSegment(sketch, "E141.7.0.2", {"start": v(-44.5, 46) * mm, "end": v(-36, 46) * mm});
            skLineSegment(sketch, "E141.7.0.3", {"start": v(-44.5, 34) * mm, "end": v(-44.5, 46) * mm});
            skLineSegment(sketch, "E141.8.0.0", {"start": v(-36, 34) * mm, "end": v(-32, 34) * mm});
            skLineSegment(sketch, "E141.8.0.1", {"start": v(-23.5, 34) * mm, "end": v(-23.5, 46) * mm});
            skLineSegment(sketch, "E141.8.0.2", {"start": v(-32, 46) * mm, "end": v(-23.5, 46) * mm});
            skLineSegment(sketch, "E141.8.0.3", {"start": v(-32, 34) * mm, "end": v(-32, 46) * mm});
            skLineSegment(sketch, "E141.9.0.0", {"start": v(-23.5, 34) * mm, "end": v(-19.5, 34) * mm});
            skLineSegment(sketch, "E141.9.0.1", {"start": v(-11, 34) * mm, "end": v(-11, 46) * mm});
            skLineSegment(sketch, "E141.9.0.2", {"start": v(-19.5, 46) * mm, "end": v(-11, 46) * mm});
            skLineSegment(sketch, "E141.9.0.3", {"start": v(-19.5, 34) * mm, "end": v(-19.5, 46) * mm});
            skLineSegment(sketch, "E141.10.0.0", {"start": v(-11, 34) * mm, "end": v(-7, 34) * mm});
            skLineSegment(sketch, "E141.10.0.1", {"start": v(1.5, 34) * mm, "end": v(1.5, 46) * mm});
            skLineSegment(sketch, "E141.10.0.2", {"start": v(-7, 46) * mm, "end": v(1.5, 46) * mm});
            skLineSegment(sketch, "E141.10.0.3", {"start": v(-7, 34) * mm, "end": v(-7, 46) * mm});
            skLineSegment(sketch, "E141.11.0.0", {"start": v(1.5, 34) * mm, "end": v(5.5, 34) * mm});
            skLineSegment(sketch, "E141.11.0.1", {"start": v(14, 34) * mm, "end": v(14, 46) * mm});
            skLineSegment(sketch, "E141.11.0.2", {"start": v(5.5, 46) * mm, "end": v(14, 46) * mm});
            skLineSegment(sketch, "E141.11.0.3", {"start": v(5.5, 34) * mm, "end": v(5.5, 46) * mm});
            skLineSegment(sketch, "E141.12.0.0", {"start": v(14, 34) * mm, "end": v(18, 34) * mm});
            skLineSegment(sketch, "E141.12.0.1", {"start": v(26.5, 34) * mm, "end": v(26.5, 46) * mm});
            skLineSegment(sketch, "E141.12.0.2", {"start": v(18, 46) * mm, "end": v(26.5, 46) * mm});
            skLineSegment(sketch, "E141.12.0.3", {"start": v(18, 34) * mm, "end": v(18, 46) * mm});
            skLineSegment(sketch, "E141.13.0.0", {"start": v(26.5, 34) * mm, "end": v(30.5, 34) * mm});
            skLineSegment(sketch, "E141.13.0.1", {"start": v(39, 34) * mm, "end": v(39, 46) * mm});
            skLineSegment(sketch, "E141.13.0.2", {"start": v(30.5, 46) * mm, "end": v(39, 46) * mm});
            skLineSegment(sketch, "E141.13.0.3", {"start": v(30.5, 34) * mm, "end": v(30.5, 46) * mm});
            skLineSegment(sketch, "E141.14.0.0", {"start": v(39, 34) * mm, "end": v(43, 34) * mm});
            skLineSegment(sketch, "E141.14.0.1", {"start": v(51.5, 34) * mm, "end": v(51.5, 46) * mm});
            skLineSegment(sketch, "E141.14.0.2", {"start": v(43, 46) * mm, "end": v(51.5, 46) * mm});
            skLineSegment(sketch, "E141.14.0.3", {"start": v(43, 34) * mm, "end": v(43, 46) * mm});
            skLineSegment(sketch, "E141.15.0.0", {"start": v(51.5, 34) * mm, "end": v(55.5, 34) * mm});
            skLineSegment(sketch, "E141.15.0.1", {"start": v(64, 34) * mm, "end": v(64, 46) * mm});
            skLineSegment(sketch, "E141.15.0.2", {"start": v(55.5, 46) * mm, "end": v(64, 46) * mm});
            skLineSegment(sketch, "E141.15.0.3", {"start": v(55.5, 34) * mm, "end": v(55.5, 46) * mm});
            skLineSegment(sketch, "E141.16.0.0", {"start": v(64, 34) * mm, "end": v(68, 34) * mm});
            skLineSegment(sketch, "E141.16.0.1", {"start": v(76.5, 34) * mm, "end": v(76.5, 46) * mm});
            skLineSegment(sketch, "E141.16.0.2", {"start": v(68, 46) * mm, "end": v(76.5, 46) * mm});
            skLineSegment(sketch, "E141.16.0.3", {"start": v(68, 34) * mm, "end": v(68, 46) * mm});
            skLineSegment(sketch, "E141.17.0.0", {"start": v(76.5, 34) * mm, "end": v(80.5, 34) * mm});
            skLineSegment(sketch, "E141.17.0.1", {"start": v(89, 34) * mm, "end": v(89, 46) * mm});
            skLineSegment(sketch, "E141.17.0.2", {"start": v(80.5, 46) * mm, "end": v(89, 46) * mm});
            skLineSegment(sketch, "E141.17.0.3", {"start": v(80.5, 34) * mm, "end": v(80.5, 46) * mm});
            skLineSegment(sketch, "E141.18.0.0", {"start": v(89, 34) * mm, "end": v(93, 34) * mm});
            skLineSegment(sketch, "E141.18.0.1", {"start": v(101.5, 34) * mm, "end": v(101.5, 46) * mm});
            skLineSegment(sketch, "E141.18.0.2", {"start": v(93, 46) * mm, "end": v(101.5, 46) * mm});
            skLineSegment(sketch, "E141.18.0.3", {"start": v(93, 34) * mm, "end": v(93, 46) * mm});
            skLineSegment(sketch, "E141.19.0.0", {"start": v(101.5, 34) * mm, "end": v(105.5, 34) * mm});
            skLineSegment(sketch, "E141.19.0.1", {"start": v(114, 34) * mm, "end": v(114, 46) * mm});
            skLineSegment(sketch, "E141.19.0.2", {"start": v(105.5, 46) * mm, "end": v(114, 46) * mm});
            skLineSegment(sketch, "E141.19.0.3", {"start": v(105.5, 34) * mm, "end": v(105.5, 46) * mm});
            skLineSegment(sketch, "E141.20.0.0", {"start": v(114, 34) * mm, "end": v(118, 34) * mm});
            skLineSegment(sketch, "E141.20.0.1", {"start": v(126.5, 34) * mm, "end": v(126.5, 46) * mm});
            skLineSegment(sketch, "E141.20.0.2", {"start": v(118, 46) * mm, "end": v(126.5, 46) * mm});
            skLineSegment(sketch, "E141.20.0.3", {"start": v(118, 34) * mm, "end": v(118, 46) * mm});
            skLineSegment(sketch, "E142.MirrorCS", {"start": v(151, 34) * mm, "end": v(155, 34) * mm});
            skLineSegment(sketch, "E143.MirrorCS", {"start": v(151, 16) * mm, "end": v(155, 16) * mm});
            skLineSegment(sketch, "E144.MirrorCS", {"start": v(151, 16) * mm, "end": v(151, 4) * mm});
            skLineSegment(sketch, "E145", {"start": v(151, 46) * mm, "end": v(130.5, 46) * mm});
            skLineSegment(sketch, "E146", {"start": v(-151, 4) * mm, "end": v(151, 4) * mm});
            skLineSegment(sketch, "E147.bottom", {"start": v(-109, 4) * mm, "end": v(-89, 4) * mm});
            skLineSegment(sketch, "E147.top", {"start": v(-109, 0) * mm, "end": v(-89, 0) * mm});
            skLineSegment(sketch, "E147.left", {"start": v(-109, 4) * mm, "end": v(-109, 0) * mm});
            skLineSegment(sketch, "E147.right", {"start": v(-89, 4) * mm, "end": v(-89, 0) * mm});
            skLineSegment(sketch, "E148.1.0.0", {"start": v(-43, 0) * mm, "end": v(-23, 0) * mm});
            skLineSegment(sketch, "E148.1.0.1", {"start": v(-43, 4) * mm, "end": v(-23, 4) * mm});
            skLineSegment(sketch, "E148.1.0.2", {"start": v(-23, 4) * mm, "end": v(-23, 0) * mm});
            skLineSegment(sketch, "E148.1.0.3", {"start": v(-43, 4) * mm, "end": v(-43, 0) * mm});
            skLineSegment(sketch, "E148.2.0.0", {"start": v(23, 0) * mm, "end": v(43, 0) * mm});
            skLineSegment(sketch, "E148.2.0.1", {"start": v(23, 4) * mm, "end": v(43, 4) * mm});
            skLineSegment(sketch, "E148.2.0.2", {"start": v(43, 4) * mm, "end": v(43, 0) * mm});
            skLineSegment(sketch, "E148.2.0.3", {"start": v(23, 4) * mm, "end": v(23, 0) * mm});
            skLineSegment(sketch, "E148.3.0.0", {"start": v(89, 0) * mm, "end": v(109, 0) * mm});
            skLineSegment(sketch, "E148.3.0.1", {"start": v(89, 4) * mm, "end": v(109, 4) * mm});
            skLineSegment(sketch, "E148.3.0.2", {"start": v(109, 4) * mm, "end": v(109, 0) * mm});
            skLineSegment(sketch, "E148.3.0.3", {"start": v(89, 4) * mm, "end": v(89, 0) * mm});
            skLineSegment(sketch, "E148.direction1", {"start": v(-109, 0) * mm, "end": v(-43, 0) * mm, "construction": true});
            skLineSegment(sketch, "E149.bottom", {"start": v(14, 26) * mm, "end": v(18, 26) * mm});
            skLineSegment(sketch, "E149.top", {"start": v(14, 14) * mm, "end": v(18, 14) * mm});
            skLineSegment(sketch, "E149.left", {"start": v(14, 26) * mm, "end": v(14, 14) * mm});
            skLineSegment(sketch, "E149.right", {"start": v(18, 26) * mm, "end": v(18, 14) * mm});
            skLineSegment(sketch, "E150.bottom", {"start": v(43, 26) * mm, "end": v(47, 26) * mm});
            skLineSegment(sketch, "E150.top", {"start": v(43, 14) * mm, "end": v(47, 14) * mm});
            skLineSegment(sketch, "E150.left", {"start": v(43, 26) * mm, "end": v(43, 14) * mm});
            skLineSegment(sketch, "E150.right", {"start": v(47, 26) * mm, "end": v(47, 14) * mm});
            skLineSegment(sketch, "E151", {"start": v(-151, 34) * mm, "end": v(-151, 46) * mm});
            skLineSegment(sketch, "E152", {"start": v(151, 46) * mm, "end": v(151, 34) * mm});
            skLineSegment(sketch, "E153", {"start": v(-151, 46) * mm, "end": v(-136, 46) * mm});
            skSolve(sketch);
        }
        {
            var Q0;
            Q0=qSketchRegion(id+"F5",true);
            extrude(context, id + "F6", {"entities" : qUnion([Q0]), "oppositeDirection" : true, "depth" : 4 * mm});
        }
        {
            var Q0;
            Q0=qCreatedBy(makeId("Front.planeOp"),FACE);
            var sketch = newSketch(context, id + "F7", { "sketchPlane" : qUnion([Q0])});
            skLineSegment(sketch, "E154", {"start": v(-57, 46) * mm, "end": v(-63, 46) * mm, "construction": true});
            skLineSegment(sketch, "E155", {"start": v(-63, 46) * mm, "end": v(-63, 26) * mm});
            skLineSegment(sketch, "E156", {"start": v(-63, 26) * mm, "end": v(-67, 26) * mm});
            skLineSegment(sketch, "E157", {"start": v(-67, 26) * mm, "end": v(-67, 14) * mm});
            skLineSegment(sketch, "E158", {"start": v(-67, 14) * mm, "end": v(-63, 14) * mm});
            skLineSegment(sketch, "E159", {"start": v(-63, 14) * mm, "end": v(-63, 4) * mm});
            skLineSegment(sketch, "E160", {"start": v(-63, 4) * mm, "end": v(-29, 4) * mm});
            skLineSegment(sketch, "E161", {"start": v(-29, 4) * mm, "end": v(-29, 0) * mm});
            skLineSegment(sketch, "E162", {"start": v(-29, 0) * mm, "end": v(-9, 0) * mm});
            skLineSegment(sketch, "E163", {"start": v(-9, 0) * mm, "end": v(-9, 4) * mm});
            skLineSegment(sketch, "E164", {"start": v(-9, 4) * mm, "end": v(25, 4) * mm});
            skLineSegment(sketch, "E165", {"start": v(25, 4) * mm, "end": v(25, 14) * mm});
            skLineSegment(sketch, "E166", {"start": v(25, 14) * mm, "end": v(29, 14) * mm});
            skLineSegment(sketch, "E167", {"start": v(29, 14) * mm, "end": v(29, 26) * mm});
            skLineSegment(sketch, "E168", {"start": v(29, 26) * mm, "end": v(25, 26) * mm});
            skLineSegment(sketch, "E169", {"start": v(25, 26) * mm, "end": v(25, 46) * mm});
            skLineSegment(sketch, "E170", {"start": v(25, 46) * mm, "end": v(19, 46) * mm, "construction": true});
            skLineSegment(sketch, "E171", {"start": v(-26, 46) * mm, "end": v(-19, 46) * mm, "construction": true});
            skLineSegment(sketch, "E172", {"start": v(-19, 46) * mm, "end": v(-12, 46) * mm, "construction": true});
            skLineSegment(sketch, "E173", {"start": v(-57, 46) * mm, "end": v(-26, 46) * mm, "construction": true});
            skLineSegment(sketch, "E174", {"start": v(-12, 46) * mm, "end": v(19, 46) * mm, "construction": true});
            skLineSegment(sketch, "E175", {"start": v(-19, 53.52) * mm, "end": v(-19, -5.95) * mm, "construction": true});
            skLineSegment(sketch, "E176.bottom", {"start": v(-21, 26) * mm, "end": v(-17, 26) * mm});
            skLineSegment(sketch, "E176.top", {"start": v(-21, 14) * mm, "end": v(-17, 14) * mm});
            skLineSegment(sketch, "E176.left", {"start": v(-21, 26) * mm, "end": v(-21, 14) * mm});
            skLineSegment(sketch, "E176.right", {"start": v(-17, 26) * mm, "end": v(-17, 14) * mm});
            skLineSegment(sketch, "E177", {"start": v(-63, 46) * mm, "end": v(-60.59, 46) * mm});
            skLineSegment(sketch, "E178", {"start": v(-22.41, 46) * mm, "end": v(-19, 46) * mm});
            skArc(sketch, "E179", {"start": v(-56.67, 42.82) * mm, "mid": v(-41.5, 30.5) * mm, "end": v(-26.33, 42.82) * mm});
            skPoint(sketch, "E180.visualSharp", {"position": v(-57, 46) * mm});
            skArc(sketch, "E180.filletArc", {"start": v(-56.67, 42.82) * mm, "mid": v(-58.06, 45.1) * mm, "end": v(-60.59, 46) * mm});
            skPoint(sketch, "E181.visualSharp", {"position": v(-26, 46) * mm});
            skArc(sketch, "E181.filletArc", {"start": v(-22.41, 46) * mm, "mid": v(-24.94, 45.1) * mm, "end": v(-26.33, 42.82) * mm});
            skLineSegment(sketch, "E182", {"start": v(-19, 46) * mm, "end": v(-15.44, 46) * mm});
            skLineSegment(sketch, "E183", {"start": v(22.73, 46) * mm, "end": v(25, 46) * mm});
            skArc(sketch, "E184", {"start": v(-11.52, 42.82) * mm, "mid": v(3.65, 30.5) * mm, "end": v(18.82, 42.82) * mm});
            skLineSegment(sketch, "E185", {"start": v(-11.85, 46) * mm, "end": v(19.15, 46) * mm, "construction": true});
            skPoint(sketch, "E186.visualSharp", {"position": v(-11.85, 46) * mm});
            skArc(sketch, "E186.filletArc", {"start": v(-11.52, 42.82) * mm, "mid": v(-12.92, 45.1) * mm, "end": v(-15.44, 46) * mm});
            skPoint(sketch, "E187.visualSharp", {"position": v(19.15, 46) * mm});
            skArc(sketch, "E187.filletArc", {"start": v(22.73, 46) * mm, "mid": v(20.21, 45.1) * mm, "end": v(18.82, 42.82) * mm});
            skSolve(sketch);
        }
        {
            var Q0;
            Q0=qSketchRegion(id+"F7",true);
            extrude(context, id + "F8", {"entities" : qUnion([Q0]), "depth" : 4 * mm});
        }
        {
            var Q0;
            Q0=qCreatedBy(makeId("Right.planeOp"),FACE);
            var sketch = newSketch(context, id + "F9", { "sketchPlane" : qUnion([Q0])});
            skLineSegment(sketch, "E188.bottom", {"start": v(18, 46) * mm, "end": v(43, 46) * mm});
            skLineSegment(sketch, "E188.top", {"start": v(18, 4) * mm, "end": v(43, 4) * mm});
            skLineSegment(sketch, "E188.left", {"start": v(18, 46) * mm, "end": v(18, 4) * mm});
            skLineSegment(sketch, "E188.right", {"start": v(43, 46) * mm, "end": v(43, 4) * mm});
            skLineSegment(sketch, "E189.bottom", {"start": v(18, 26) * mm, "end": v(14, 26) * mm});
            skLineSegment(sketch, "E189.top", {"start": v(18, 14) * mm, "end": v(14, 14) * mm});
            skLineSegment(sketch, "E189.left", {"start": v(18, 26) * mm, "end": v(18, 14) * mm});
            skLineSegment(sketch, "E189.right", {"start": v(14, 26) * mm, "end": v(14, 14) * mm});
            skPoint(sketch, "E190.firstSnap0", {"position": v(16, 14) * mm});
            skLineSegment(sketch, "E190.bottom", {"start": v(43, 14) * mm, "end": v(47, 14) * mm});
            skLineSegment(sketch, "E190.top", {"start": v(43, 26) * mm, "end": v(47, 26) * mm});
            skLineSegment(sketch, "E190.left", {"start": v(43, 14) * mm, "end": v(43, 26) * mm});
            skLineSegment(sketch, "E190.right", {"start": v(47, 14) * mm, "end": v(47, 26) * mm});
            skSolve(sketch);
        }
        {
            var Q0;
            Q0=qSketchRegion(id+"F9",true);
            extrude(context, id + "F10", {"entities" : qUnion([Q0]), "depth" : 4 * mm});
        }
        {
            var Q0;
            Q0=qCreatedBy(makeId("Front.planeOp"),FACE);
            var sketch = newSketch(context, id + "F11", { "sketchPlane" : qUnion([Q0])});
            skLineSegment(sketch, "E191.top", {"start": v(-106, 4) * mm, "end": v(106, 4) * mm});
            skLineSegment(sketch, "E191.left", {"start": v(-106, 46) * mm, "end": v(-106, 4) * mm});
            skLineSegment(sketch, "E191.right", {"start": v(106, 46) * mm, "end": v(106, 4) * mm});
            skLineSegment(sketch, "E192", {"start": v(106, 46) * mm, "end": v(90.5, 46) * mm, "construction": true});
            skLineSegment(sketch, "E193", {"start": v(-101.5, 46) * mm, "end": v(-106, 46) * mm});
            skArc(sketch, "E194", {"start": v(44.5, 46) * mm, "mid": v(67.5, 23) * mm, "end": v(90.5, 46) * mm, "construction": true});
            skLineSegment(sketch, "E195", {"start": v(29, 65.47) * mm, "end": v(29, 0) * mm, "construction": true});
            skLineSegment(sketch, "E196", {"start": v(-67, 0) * mm, "end": v(-67, 80.2) * mm, "construction": true});
            skLineSegment(sketch, "E197", {"start": v(44.5, 46) * mm, "end": v(29, 46) * mm, "construction": true});
            skLineSegment(sketch, "E198", {"start": v(29, 46) * mm, "end": v(-67, 46) * mm});
            skLineSegment(sketch, "E199", {"start": v(-67, 46) * mm, "end": v(-71.5, 46) * mm});
            skLineSegment(sketch, "E200", {"start": v(110, 23) * mm, "end": v(-110, 23) * mm, "construction": true});
            skLineSegment(sketch, "E201", {"start": v(-75.5, 42) * mm, "end": v(-75.5, 34) * mm});
            skLineSegment(sketch, "E202", {"start": v(-97.5, 42) * mm, "end": v(-97.5, 34) * mm});
            skArc(sketch, "E203", {"start": v(-97.5, 34) * mm, "mid": v(-86.5, 23) * mm, "end": v(-75.5, 34) * mm});
            skLineSegment(sketch, "E204", {"start": v(-75.5, 34) * mm, "end": v(-97.5, 34) * mm, "construction": true});
            skLineSegment(sketch, "E205", {"start": v(90.5, 46) * mm, "end": v(90.5, 23) * mm, "construction": true});
            skLineSegment(sketch, "E206", {"start": v(90.5, 23) * mm, "end": v(90.5, 0) * mm, "construction": true});
            skPoint(sketch, "E207.oppositeSnap0", {"position": v(90.5, 11.5) * mm});
            skLineSegment(sketch, "E208", {"start": v(16, 40) * mm, "end": v(-16, 40) * mm});
            skLineSegment(sketch, "E209", {"start": v(0, 40) * mm, "end": v(0, 0) * mm, "construction": true});
            skArc(sketch, "E210", {"start": v(-16, 40) * mm, "mid": v(0, 30.25) * mm, "end": v(16, 40) * mm});
            skLineSegment(sketch, "E211.bottom", {"start": v(-88, 4) * mm, "end": v(-77, 4) * mm});
            skLineSegment(sketch, "E211.top", {"start": v(-88, 0) * mm, "end": v(-77, 0) * mm});
            skLineSegment(sketch, "E211.left", {"start": v(-88, 4) * mm, "end": v(-88, 0) * mm});
            skLineSegment(sketch, "E211.right", {"start": v(-77, 4) * mm, "end": v(-77, 0) * mm});
            skLineSegment(sketch, "E212.bottom", {"start": v(-55, 4) * mm, "end": v(-44, 4) * mm});
            skLineSegment(sketch, "E212.top", {"start": v(-55, 0) * mm, "end": v(-44, 0) * mm});
            skLineSegment(sketch, "E212.left", {"start": v(-55, 4) * mm, "end": v(-55, 0) * mm});
            skLineSegment(sketch, "E212.right", {"start": v(-44, 4) * mm, "end": v(-44, 0) * mm});
            skLineSegment(sketch, "E213.bottom", {"start": v(-22, 4) * mm, "end": v(-11, 4) * mm});
            skLineSegment(sketch, "E213.top", {"start": v(-22, 0) * mm, "end": v(-11, 0) * mm});
            skLineSegment(sketch, "E213.left", {"start": v(-22, 4) * mm, "end": v(-22, 0) * mm});
            skLineSegment(sketch, "E213.right", {"start": v(-11, 4) * mm, "end": v(-11, 0) * mm});
            skLineSegment(sketch, "E214.bottom", {"start": v(11, 4) * mm, "end": v(22, 4) * mm});
            skLineSegment(sketch, "E214.top", {"start": v(11, 0) * mm, "end": v(22, 0) * mm});
            skLineSegment(sketch, "E214.left", {"start": v(11, 4) * mm, "end": v(11, 0) * mm});
            skLineSegment(sketch, "E214.right", {"start": v(22, 4) * mm, "end": v(22, 0) * mm});
            skLineSegment(sketch, "E215.bottom", {"start": v(44, 4) * mm, "end": v(55, 4) * mm});
            skLineSegment(sketch, "E215.top", {"start": v(44, 0) * mm, "end": v(55, 0) * mm});
            skLineSegment(sketch, "E215.left", {"start": v(44, 4) * mm, "end": v(44, 0) * mm});
            skLineSegment(sketch, "E215.right", {"start": v(55, 4) * mm, "end": v(55, 0) * mm});
            skLineSegment(sketch, "E216.bottom", {"start": v(77, 4) * mm, "end": v(88, 4) * mm});
            skLineSegment(sketch, "E216.top", {"start": v(77, 0) * mm, "end": v(88, 0) * mm});
            skLineSegment(sketch, "E216.left", {"start": v(77, 4) * mm, "end": v(77, 0) * mm});
            skLineSegment(sketch, "E216.right", {"start": v(88, 4) * mm, "end": v(88, 0) * mm});
            skLineSegment(sketch, "E217", {"start": v(106, 34) * mm, "end": v(110, 34) * mm});
            skLineSegment(sketch, "E218", {"start": v(110, 34) * mm, "end": v(110, 16) * mm});
            skLineSegment(sketch, "E219", {"start": v(110, 16) * mm, "end": v(106, 16) * mm});
            skLineSegment(sketch, "E220", {"start": v(-106, 34) * mm, "end": v(-110, 34) * mm});
            skLineSegment(sketch, "E221", {"start": v(-110, 34) * mm, "end": v(-110, 16) * mm});
            skLineSegment(sketch, "E222", {"start": v(-110, 16) * mm, "end": v(-106, 16) * mm});
            skLineSegment(sketch, "E223.bottom", {"start": v(-67, 34) * mm, "end": v(-63, 34) * mm});
            skLineSegment(sketch, "E223.top", {"start": v(-67, 16) * mm, "end": v(-63, 16) * mm});
            skLineSegment(sketch, "E223.left", {"start": v(-67, 34) * mm, "end": v(-67, 16) * mm});
            skLineSegment(sketch, "E223.right", {"start": v(-63, 34) * mm, "end": v(-63, 16) * mm});
            skLineSegment(sketch, "E224.bottom", {"start": v(29, 34) * mm, "end": v(25, 34) * mm});
            skLineSegment(sketch, "E224.top", {"start": v(29, 16) * mm, "end": v(25, 16) * mm});
            skLineSegment(sketch, "E224.left", {"start": v(29, 34) * mm, "end": v(29, 16) * mm});
            skLineSegment(sketch, "E224.right", {"start": v(25, 34) * mm, "end": v(25, 16) * mm});
            skLineSegment(sketch, "E225", {"start": v(106, 46) * mm, "end": v(94.2, 46) * mm});
            skLineSegment(sketch, "E226", {"start": v(40.8, 46) * mm, "end": v(29, 46) * mm});
            skLineSegment(sketch, "E227", {"start": v(90.5, 46) * mm, "end": v(44.5, 46) * mm, "construction": true});
            skArc(sketch, "E228", {"start": v(44.75, 42.6) * mm, "mid": v(67.5, 23) * mm, "end": v(90.25, 42.6) * mm});
            skPoint(sketch, "E229.visualSharp", {"position": v(44.5, 46) * mm});
            skArc(sketch, "E229.filletArc", {"start": v(44.75, 42.6) * mm, "mid": v(43.4, 45.03) * mm, "end": v(40.8, 46) * mm});
            skPoint(sketch, "E230.visualSharp", {"position": v(90.5, 46) * mm});
            skArc(sketch, "E230.filletArc", {"start": v(94.2, 46) * mm, "mid": v(91.6, 45.03) * mm, "end": v(90.25, 42.6) * mm});
            skLineSegment(sketch, "E231", {"start": v(67.5, 46) * mm, "end": v(60.34, 24.14) * mm, "construction": true});
            skLineSegment(sketch, "E232", {"start": v(67.5, 46) * mm, "end": v(50.22, 30.82) * mm, "construction": true});
            skPoint(sketch, "E233.visualSharp", {"position": v(-75.5, 46) * mm});
            skArc(sketch, "E233.filletArc", {"start": v(-71.5, 46) * mm, "mid": v(-74.33, 44.83) * mm, "end": v(-75.5, 42) * mm});
            skPoint(sketch, "E234.visualSharp", {"position": v(-97.5, 46) * mm});
            skArc(sketch, "E234.filletArc", {"start": v(-97.5, 42) * mm, "mid": v(-98.67, 44.83) * mm, "end": v(-101.5, 46) * mm});
            skSolve(sketch);
        }
        {
            var Q0;
            Q0=qSketchRegion(id+"F11",true);
            extrude(context, id + "F12", {"entities" : qUnion([Q0]), "depth" : 4 * mm});
        }
        {
            var Q0;
            Q0=qCreatedBy(makeId("Front.planeOp"),FACE);
            var sketch = newSketch(context, id + "F13", { "sketchPlane" : qUnion([Q0])});
            skLineSegment(sketch, "E235.top", {"start": v(-106, 4) * mm, "end": v(-88, 4) * mm});
            skLineSegment(sketch, "E236.bottom", {"start": v(-106, 34) * mm, "end": v(-110, 34) * mm});
            skLineSegment(sketch, "E236.top", {"start": v(-106, 16) * mm, "end": v(-110, 16) * mm});
            skLineSegment(sketch, "E237.bottom", {"start": v(106, 34) * mm, "end": v(110, 34) * mm});
            skLineSegment(sketch, "E237.top", {"start": v(106, 16) * mm, "end": v(110, 16) * mm});
            skLineSegment(sketch, "E238", {"start": v(29, 65.47) * mm, "end": v(29, 4) * mm, "construction": true});
            skLineSegment(sketch, "E239", {"start": v(-67, 0) * mm, "end": v(-67, 80.2) * mm, "construction": true});
            skLineSegment(sketch, "E240.bottom", {"start": v(29, 34) * mm, "end": v(25, 34) * mm});
            skLineSegment(sketch, "E240.top", {"start": v(29, 16) * mm, "end": v(25, 16) * mm});
            skLineSegment(sketch, "E240.left", {"start": v(29, 34) * mm, "end": v(29, 16) * mm});
            skLineSegment(sketch, "E240.right", {"start": v(25, 34) * mm, "end": v(25, 16) * mm});
            skLineSegment(sketch, "E241.bottom", {"start": v(-67, 34) * mm, "end": v(-63, 34) * mm});
            skLineSegment(sketch, "E241.top", {"start": v(-67, 16) * mm, "end": v(-63, 16) * mm});
            skLineSegment(sketch, "E241.left", {"start": v(-67, 34) * mm, "end": v(-67, 16) * mm});
            skLineSegment(sketch, "E241.right", {"start": v(-63, 34) * mm, "end": v(-63, 16) * mm});
            skLineSegment(sketch, "E242", {"start": v(16, 40) * mm, "end": v(-16, 40) * mm});
            skLineSegment(sketch, "E243", {"start": v(0, 40) * mm, "end": v(0, 0) * mm, "construction": true});
            skArc(sketch, "E244", {"start": v(-16, 40) * mm, "mid": v(0, 30.25) * mm, "end": v(16, 40) * mm});
            skLineSegment(sketch, "E245", {"start": v(-9, 66.76) * mm, "end": v(-9, -62.6) * mm, "construction": true});
            skLineSegment(sketch, "E246", {"start": v(-29, 66.35) * mm, "end": v(-29, -69.55) * mm, "construction": true});
            skLineSegment(sketch, "E247.bottom", {"start": v(88, 0) * mm, "end": v(77, 0) * mm});
            skLineSegment(sketch, "E247.left", {"start": v(88, 0) * mm, "end": v(88, 4) * mm});
            skLineSegment(sketch, "E247.right", {"start": v(77, 0) * mm, "end": v(77, 4) * mm});
            skLineSegment(sketch, "E248.bottom", {"start": v(55, 0) * mm, "end": v(44, 0) * mm});
            skLineSegment(sketch, "E248.left", {"start": v(55, 0) * mm, "end": v(55, 4) * mm});
            skLineSegment(sketch, "E248.right", {"start": v(44, 0) * mm, "end": v(44, 4) * mm});
            skLineSegment(sketch, "E249.bottom", {"start": v(22, 0) * mm, "end": v(11, 0) * mm});
            skLineSegment(sketch, "E249.left", {"start": v(22, 0) * mm, "end": v(22, 4) * mm});
            skLineSegment(sketch, "E249.right", {"start": v(11, 0) * mm, "end": v(11, 4) * mm});
            skLineSegment(sketch, "E250.bottom", {"start": v(-44, 0) * mm, "end": v(-55, 0) * mm});
            skLineSegment(sketch, "E250.left", {"start": v(-44, 0) * mm, "end": v(-44, 4) * mm});
            skLineSegment(sketch, "E250.right", {"start": v(-55, 0) * mm, "end": v(-55, 4) * mm});
            skLineSegment(sketch, "E251.bottom", {"start": v(-77, 0) * mm, "end": v(-88, 0) * mm});
            skLineSegment(sketch, "E251.left", {"start": v(-77, 0) * mm, "end": v(-77, 4) * mm});
            skLineSegment(sketch, "E251.right", {"start": v(-88, 0) * mm, "end": v(-88, 4) * mm});
            skLineSegment(sketch, "E252.trimOffspring", {"start": v(-9, 4) * mm, "end": v(11, 4) * mm});
            skLineSegment(sketch, "E253.trimOffspring", {"start": v(88, 4) * mm, "end": v(106, 4) * mm});
            skLineSegment(sketch, "E254.trimOffspring", {"start": v(55, 4) * mm, "end": v(77, 4) * mm});
            skLineSegment(sketch, "E255.trimOffspring", {"start": v(22, 4) * mm, "end": v(44, 4) * mm});
            skLineSegment(sketch, "E256.trimOffspring", {"start": v(-44, 4) * mm, "end": v(-29, 4) * mm});
            skLineSegment(sketch, "E257.trimOffspring", {"start": v(-77, 4) * mm, "end": v(-55, 4) * mm});
            skLineSegment(sketch, "E258.right", {"start": v(110, 46) * mm, "end": v(110, 34) * mm});
            skLineSegment(sketch, "E259.bottom", {"start": v(110, 16) * mm, "end": v(106, 16) * mm});
            skLineSegment(sketch, "E259.top", {"start": v(110, 4) * mm, "end": v(106, 4) * mm});
            skLineSegment(sketch, "E259.left", {"start": v(110, 16) * mm, "end": v(110, 4) * mm});
            skLineSegment(sketch, "E260.bottom", {"start": v(-106, 4) * mm, "end": v(-110, 4) * mm});
            skLineSegment(sketch, "E260.right", {"start": v(-110, 4) * mm, "end": v(-110, 16) * mm});
            skLineSegment(sketch, "E261.bottom", {"start": v(-110, 34) * mm, "end": v(-106, 34) * mm});
            skLineSegment(sketch, "E261.left", {"start": v(-110, 34) * mm, "end": v(-110, 46) * mm});
            skLineSegment(sketch, "E262", {"start": v(106, 34) * mm, "end": v(106, 16) * mm});
            skLineSegment(sketch, "E263", {"start": v(-106, 34) * mm, "end": v(-106, 16) * mm});
            skLineSegment(sketch, "E264", {"start": v(94.2, 46) * mm, "end": v(110, 46) * mm});
            skLineSegment(sketch, "E265", {"start": v(-71.5, 46) * mm, "end": v(40.8, 46) * mm});
            skLineSegment(sketch, "E266", {"start": v(-110, 46) * mm, "end": v(-101.5, 46) * mm});
            skLineSegment(sketch, "E267", {"start": v(-29, 4) * mm, "end": v(-29, 12) * mm});
            skLineSegment(sketch, "E268", {"start": v(-9, 4) * mm, "end": v(-9, 12) * mm});
            skArc(sketch, "E269", {"start": v(-9, 12) * mm, "mid": v(-19, 22) * mm, "end": v(-29, 12) * mm});
            skLineSegment(sketch, "E270", {"start": v(-29, 12) * mm, "end": v(-9, 12) * mm, "construction": true});
            skArc(sketch, "E271", {"start": v(44.75, 42.6) * mm, "mid": v(67.5, 23) * mm, "end": v(90.25, 42.6) * mm});
            skLineSegment(sketch, "E272", {"start": v(-75.5, 42) * mm, "end": v(-75.5, 34) * mm});
            skLineSegment(sketch, "E273", {"start": v(-97.5, 42) * mm, "end": v(-97.5, 34) * mm});
            skArc(sketch, "E274", {"start": v(-97.5, 34) * mm, "mid": v(-86.5, 23) * mm, "end": v(-75.5, 34) * mm});
            skPoint(sketch, "E275.visualSharp", {"position": v(-75.5, 46) * mm});
            skArc(sketch, "E275.filletArc", {"start": v(-71.5, 46) * mm, "mid": v(-74.33, 44.83) * mm, "end": v(-75.5, 42) * mm});
            skPoint(sketch, "E276.visualSharp", {"position": v(-97.5, 46) * mm});
            skArc(sketch, "E276.filletArc", {"start": v(-97.5, 42) * mm, "mid": v(-98.67, 44.83) * mm, "end": v(-101.5, 46) * mm});
            skPoint(sketch, "E277.visualSharp", {"position": v(90.5, 46) * mm});
            skArc(sketch, "E277.filletArc", {"start": v(94.2, 46) * mm, "mid": v(91.6, 45.03) * mm, "end": v(90.25, 42.6) * mm});
            skPoint(sketch, "E278.visualSharp", {"position": v(44.5, 46) * mm});
            skArc(sketch, "E278.filletArc", {"start": v(44.75, 42.6) * mm, "mid": v(43.4, 45.03) * mm, "end": v(40.8, 46) * mm});
            skSolve(sketch);
        }
        {
            var Q0;
            Q0=qSketchRegion(id+"F13",true);
            extrude(context, id + "F14", {"entities" : qUnion([Q0]), "oppositeDirection" : true, "depth" : 4 * mm});
        }
        {
            var Q0;
            Q0=qCreatedBy(makeId("Right.planeOp"),FACE);
            var sketch = newSketch(context, id + "F15", { "sketchPlane" : qUnion([Q0])});
            skLineSegment(sketch, "E279.bottom", {"start": v(47, 12) * mm, "end": v(151, 12) * mm});
            skLineSegment(sketch, "E279.top", {"start": v(47, 4) * mm, "end": v(151, 4) * mm});
            skLineSegment(sketch, "E279.left", {"start": v(47, 12) * mm, "end": v(47, 4) * mm});
            skLineSegment(sketch, "E279.right", {"start": v(151, 12) * mm, "end": v(151, 4) * mm});
            skLineSegment(sketch, "E280.bottom", {"start": v(89, 4) * mm, "end": v(109, 4) * mm});
            skLineSegment(sketch, "E280.top", {"start": v(89, 0) * mm, "end": v(109, 0) * mm});
            skLineSegment(sketch, "E280.left", {"start": v(89, 4) * mm, "end": v(89, 0) * mm});
            skLineSegment(sketch, "E280.right", {"start": v(109, 4) * mm, "end": v(109, 0) * mm});
            skSolve(sketch);
        }
        {
            var Q0;
            Q0=qSketchRegion(id+"F15",true);
            extrude(context, id + "F16", {"entities" : qUnion([Q0]), "depth" : 4 * mm});
        }
        {
            var Q0;
            Q0=qCreatedBy(makeId("Top.planeOp"),FACE);
            var sketch = newSketch(context, id + "F17", { "sketchPlane" : qUnion([Q0])});
            skLineSegment(sketch, "E281.bottom", {"start": v(-59, 146.5) * mm, "end": v(20.5, 146.5) * mm});
            skLineSegment(sketch, "E281.top", {"start": v(-59, 51) * mm, "end": v(20.5, 51) * mm});
            skLineSegment(sketch, "E281.left", {"start": v(-59, 146.5) * mm, "end": v(-59, 51) * mm});
            skLineSegment(sketch, "E281.right", {"start": v(20.5, 146.5) * mm, "end": v(20.5, 51) * mm});
            skLineSegment(sketch, "E282.bottom", {"start": v(20.5, 150.5) * mm, "end": v(24.5, 150.5) * mm});
            skLineSegment(sketch, "E282.top", {"start": v(20.5, 137.5) * mm, "end": v(24.5, 137.5) * mm});
            skLineSegment(sketch, "E282.left", {"start": v(20.5, 150.5) * mm, "end": v(20.5, 137.5) * mm});
            skLineSegment(sketch, "E282.right", {"start": v(24.5, 150.5) * mm, "end": v(24.5, 137.5) * mm});
            skLineSegment(sketch, "E283.bottom", {"start": v(12.4, 146.5) * mm, "end": v(24.5, 146.5) * mm});
            skLineSegment(sketch, "E283.top", {"start": v(12.4, 150.5) * mm, "end": v(24.5, 150.5) * mm});
            skLineSegment(sketch, "E283.left", {"start": v(12.4, 146.5) * mm, "end": v(12.4, 150.5) * mm});
            skLineSegment(sketch, "E283.right", {"start": v(24.5, 146.5) * mm, "end": v(24.5, 150.5) * mm});
            skLineSegment(sketch, "E284.1.0.0", {"start": v(-12.73, 150.5) * mm, "end": v(-0.63, 150.5) * mm});
            skLineSegment(sketch, "E284.1.0.1", {"start": v(-12.73, 146.5) * mm, "end": v(-0.63, 146.5) * mm});
            skLineSegment(sketch, "E284.1.0.2", {"start": v(-12.73, 146.5) * mm, "end": v(-12.73, 150.5) * mm});
            skLineSegment(sketch, "E284.1.0.3", {"start": v(-0.63, 146.5) * mm, "end": v(-0.63, 150.5) * mm});
            skLineSegment(sketch, "E284.1.0.4", {"start": v(-4.63, 150.5) * mm, "end": v(-0.63, 150.5) * mm});
            skLineSegment(sketch, "E284.2.0.0", {"start": v(-37.87, 150.5) * mm, "end": v(-25.77, 150.5) * mm});
            skLineSegment(sketch, "E284.2.0.1", {"start": v(-37.87, 146.5) * mm, "end": v(-25.77, 146.5) * mm});
            skLineSegment(sketch, "E284.2.0.2", {"start": v(-37.87, 146.5) * mm, "end": v(-37.87, 150.5) * mm});
            skLineSegment(sketch, "E284.2.0.3", {"start": v(-25.77, 146.5) * mm, "end": v(-25.77, 150.5) * mm});
            skLineSegment(sketch, "E284.2.0.4", {"start": v(-29.77, 150.5) * mm, "end": v(-25.77, 150.5) * mm});
            skLineSegment(sketch, "E284.3.0.0", {"start": v(-50.9, 150.5) * mm, "end": v(-63, 150.5) * mm});
            skLineSegment(sketch, "E284.3.0.1", {"start": v(-63, 146.5) * mm, "end": v(-50.9, 146.5) * mm});
            skLineSegment(sketch, "E284.3.0.2", {"start": v(-63, 146.5) * mm, "end": v(-63, 150.5) * mm});
            skLineSegment(sketch, "E284.3.0.3", {"start": v(-50.9, 146.5) * mm, "end": v(-50.9, 150.5) * mm});
            skLineSegment(sketch, "E284.3.0.4", {"start": v(-54.9, 150.5) * mm, "end": v(-50.9, 150.5) * mm});
            skLineSegment(sketch, "E284.direction1", {"start": v(12.4, 146.5) * mm, "end": v(-12.73, 146.5) * mm, "construction": true});
            skLineSegment(sketch, "E285.0.1.0", {"start": v(24.5, 127.87) * mm, "end": v(24.5, 114.87) * mm});
            skLineSegment(sketch, "E285.0.1.1", {"start": v(24.5, 123.87) * mm, "end": v(24.5, 127.87) * mm});
            skLineSegment(sketch, "E285.0.1.2", {"start": v(20.5, 127.87) * mm, "end": v(20.5, 114.87) * mm});
            skLineSegment(sketch, "E285.0.1.3", {"start": v(20.5, 114.87) * mm, "end": v(24.5, 114.87) * mm});
            skLineSegment(sketch, "E285.0.1.4", {"start": v(20.5, 127.87) * mm, "end": v(24.5, 127.87) * mm});
            skLineSegment(sketch, "E285.0.2.0", {"start": v(24.5, 105.25) * mm, "end": v(24.5, 92.25) * mm});
            skLineSegment(sketch, "E285.0.2.1", {"start": v(24.5, 101.25) * mm, "end": v(24.5, 105.25) * mm});
            skLineSegment(sketch, "E285.0.2.2", {"start": v(20.5, 105.25) * mm, "end": v(20.5, 92.25) * mm});
            skLineSegment(sketch, "E285.0.2.3", {"start": v(20.5, 92.25) * mm, "end": v(24.5, 92.25) * mm});
            skLineSegment(sketch, "E285.0.2.4", {"start": v(20.5, 105.25) * mm, "end": v(24.5, 105.25) * mm});
            skLineSegment(sketch, "E285.0.3.0", {"start": v(24.5, 82.62) * mm, "end": v(24.5, 69.62) * mm});
            skLineSegment(sketch, "E285.0.3.1", {"start": v(24.5, 78.62) * mm, "end": v(24.5, 82.62) * mm});
            skLineSegment(sketch, "E285.0.3.2", {"start": v(20.5, 82.62) * mm, "end": v(20.5, 69.62) * mm});
            skLineSegment(sketch, "E285.0.3.3", {"start": v(20.5, 69.62) * mm, "end": v(24.5, 69.62) * mm});
            skLineSegment(sketch, "E285.0.3.4", {"start": v(20.5, 82.62) * mm, "end": v(24.5, 82.62) * mm});
            skLineSegment(sketch, "E285.0.4.0", {"start": v(24.5, 47) * mm, "end": v(24.5, 60) * mm});
            skLineSegment(sketch, "E285.0.4.1", {"start": v(24.5, 56) * mm, "end": v(24.5, 60) * mm});
            skLineSegment(sketch, "E285.0.4.2", {"start": v(20.5, 60) * mm, "end": v(20.5, 47) * mm});
            skLineSegment(sketch, "E285.0.4.3", {"start": v(20.5, 47) * mm, "end": v(24.5, 47) * mm});
            skLineSegment(sketch, "E285.0.4.4", {"start": v(20.5, 60) * mm, "end": v(24.5, 60) * mm});
            skLineSegment(sketch, "E285.direction1", {"start": v(20.5, 137.5) * mm, "end": v(41, 137.5) * mm, "construction": true});
            skLineSegment(sketch, "E285.direction2", {"start": v(20.5, 137.5) * mm, "end": v(20.5, 114.87) * mm, "construction": true});
            skLineSegment(sketch, "E286.bottom", {"start": v(-59, 137.5) * mm, "end": v(-63, 137.5) * mm});
            skLineSegment(sketch, "E286.top", {"start": v(-59, 150.5) * mm, "end": v(-63, 150.5) * mm});
            skLineSegment(sketch, "E286.left", {"start": v(-59, 137.5) * mm, "end": v(-59, 150.5) * mm});
            skLineSegment(sketch, "E286.right", {"start": v(-63, 137.5) * mm, "end": v(-63, 150.5) * mm});
            skLineSegment(sketch, "E287.0.1.0", {"start": v(-59, 114.87) * mm, "end": v(-59, 127.87) * mm});
            skLineSegment(sketch, "E287.0.1.1", {"start": v(-63, 114.87) * mm, "end": v(-63, 127.87) * mm});
            skLineSegment(sketch, "E287.0.1.2", {"start": v(-59, 127.87) * mm, "end": v(-63, 127.87) * mm});
            skLineSegment(sketch, "E287.0.1.3", {"start": v(-59, 114.87) * mm, "end": v(-63, 114.87) * mm});
            skLineSegment(sketch, "E287.0.1.4", {"start": v(-63, 123.87) * mm, "end": v(-63, 127.87) * mm});
            skLineSegment(sketch, "E287.0.2.0", {"start": v(-59, 92.25) * mm, "end": v(-59, 105.25) * mm});
            skLineSegment(sketch, "E287.0.2.1", {"start": v(-63, 92.25) * mm, "end": v(-63, 105.25) * mm});
            skLineSegment(sketch, "E287.0.2.2", {"start": v(-59, 105.25) * mm, "end": v(-63, 105.25) * mm});
            skLineSegment(sketch, "E287.0.2.3", {"start": v(-59, 92.25) * mm, "end": v(-63, 92.25) * mm});
            skLineSegment(sketch, "E287.0.2.4", {"start": v(-63, 101.25) * mm, "end": v(-63, 105.25) * mm});
            skLineSegment(sketch, "E287.0.3.0", {"start": v(-59, 69.62) * mm, "end": v(-59, 82.62) * mm});
            skLineSegment(sketch, "E287.0.3.1", {"start": v(-63, 69.62) * mm, "end": v(-63, 82.62) * mm});
            skLineSegment(sketch, "E287.0.3.2", {"start": v(-59, 82.62) * mm, "end": v(-63, 82.62) * mm});
            skLineSegment(sketch, "E287.0.3.3", {"start": v(-59, 69.62) * mm, "end": v(-63, 69.62) * mm});
            skLineSegment(sketch, "E287.0.3.4", {"start": v(-63, 78.62) * mm, "end": v(-63, 82.62) * mm});
            skLineSegment(sketch, "E287.0.4.0", {"start": v(-59, 47) * mm, "end": v(-59, 60) * mm});
            skLineSegment(sketch, "E287.0.4.1", {"start": v(-63, 47) * mm, "end": v(-63, 60) * mm});
            skLineSegment(sketch, "E287.0.4.2", {"start": v(-59, 60) * mm, "end": v(-63, 60) * mm});
            skLineSegment(sketch, "E287.0.4.3", {"start": v(-59, 47) * mm, "end": v(-63, 47) * mm});
            skLineSegment(sketch, "E287.0.4.4", {"start": v(-63, 56) * mm, "end": v(-63, 60) * mm});
            skLineSegment(sketch, "E287.direction1", {"start": v(-63, 137.5) * mm, "end": v(-34, 137.5) * mm, "construction": true});
            skLineSegment(sketch, "E287.direction2", {"start": v(-63, 137.5) * mm, "end": v(-63, 114.87) * mm, "construction": true});
            skLineSegment(sketch, "E288.bottom", {"start": v(-63, 47) * mm, "end": v(-50.9, 47) * mm});
            skLineSegment(sketch, "E288.top", {"start": v(-63, 51) * mm, "end": v(-50.9, 51) * mm});
            skLineSegment(sketch, "E288.left", {"start": v(-63, 47) * mm, "end": v(-63, 51) * mm});
            skLineSegment(sketch, "E288.right", {"start": v(-50.9, 47) * mm, "end": v(-50.9, 51) * mm});
            skLineSegment(sketch, "E289.1.0.0", {"start": v(-37.87, 47) * mm, "end": v(-37.87, 51) * mm});
            skLineSegment(sketch, "E289.1.0.1", {"start": v(-37.87, 47) * mm, "end": v(-25.77, 47) * mm});
            skLineSegment(sketch, "E289.1.0.2", {"start": v(-25.77, 47) * mm, "end": v(-25.77, 51) * mm});
            skLineSegment(sketch, "E289.1.0.3", {"start": v(-37.87, 51) * mm, "end": v(-25.77, 51) * mm});
            skLineSegment(sketch, "E289.1.0.4", {"start": v(-33.87, 47) * mm, "end": v(-37.87, 47) * mm});
            skLineSegment(sketch, "E289.2.0.0", {"start": v(-12.73, 47) * mm, "end": v(-12.73, 51) * mm});
            skLineSegment(sketch, "E289.2.0.1", {"start": v(-12.73, 47) * mm, "end": v(-0.63, 47) * mm});
            skLineSegment(sketch, "E289.2.0.2", {"start": v(-0.63, 47) * mm, "end": v(-0.63, 51) * mm});
            skLineSegment(sketch, "E289.2.0.3", {"start": v(-12.73, 51) * mm, "end": v(-0.63, 51) * mm});
            skLineSegment(sketch, "E289.2.0.4", {"start": v(-8.73, 47) * mm, "end": v(-12.73, 47) * mm});
            skLineSegment(sketch, "E289.3.0.0", {"start": v(12.4, 47) * mm, "end": v(12.4, 51) * mm});
            skLineSegment(sketch, "E289.3.0.1", {"start": v(12.4, 47) * mm, "end": v(24.5, 47) * mm});
            skLineSegment(sketch, "E289.3.0.2", {"start": v(24.5, 47) * mm, "end": v(24.5, 51) * mm});
            skLineSegment(sketch, "E289.3.0.3", {"start": v(12.4, 51) * mm, "end": v(24.5, 51) * mm});
            skLineSegment(sketch, "E289.3.0.4", {"start": v(16.4, 47) * mm, "end": v(12.4, 47) * mm});
            skLineSegment(sketch, "E289.direction1", {"start": v(-63, 47) * mm, "end": v(-37.87, 47) * mm, "construction": true});
            skLineSegment(sketch, "E290", {"start": v(-19.25, 146.5) * mm, "end": v(-19.25, 125.62) * mm, "construction": true});
            skLineSegment(sketch, "E291.bottom", {"start": v(-32.5, 100.75) * mm, "end": v(-6, 100.75) * mm});
            skLineSegment(sketch, "E291.top", {"start": v(-32.5, 96.75) * mm, "end": v(-6, 96.75) * mm});
            skLineSegment(sketch, "E291.left", {"start": v(-32.5, 100.75) * mm, "end": v(-32.5, 96.75) * mm});
            skLineSegment(sketch, "E291.right", {"start": v(-6, 100.75) * mm, "end": v(-6, 96.75) * mm});
            skLineSegment(sketch, "E292.bottom", {"start": v(-32.5, 125.62) * mm, "end": v(-6, 125.62) * mm});
            skLineSegment(sketch, "E292.top", {"start": v(-32.5, 121.62) * mm, "end": v(-6, 121.62) * mm});
            skLineSegment(sketch, "E292.left", {"start": v(-32.5, 125.62) * mm, "end": v(-32.5, 121.62) * mm});
            skLineSegment(sketch, "E292.right", {"start": v(-6, 125.62) * mm, "end": v(-6, 121.62) * mm});
            skLineSegment(sketch, "E293", {"start": v(-32.5, 100.75) * mm, "end": v(-59, 100.75) * mm, "construction": true});
            skLineSegment(sketch, "E294", {"start": v(-6, 100.75) * mm, "end": v(20.5, 100.75) * mm, "construction": true});
            skLineSegment(sketch, "E295", {"start": v(-19.25, 121.62) * mm, "end": v(-19.25, 100.75) * mm, "construction": true});
            skLineSegment(sketch, "E296", {"start": v(-19.25, 96.75) * mm, "end": v(-19.25, 75.87) * mm, "construction": true});
            skLineSegment(sketch, "E297", {"start": v(-19.25, 71.87) * mm, "end": v(-19.25, 51) * mm, "construction": true});
            skLineSegment(sketch, "E298", {"start": v(-59, 75.87) * mm, "end": v(20.5, 75.87) * mm, "construction": true});
            skLineSegment(sketch, "E299", {"start": v(20.5, 71.87) * mm, "end": v(-59, 71.87) * mm, "construction": true});
            skSolve(sketch);
        }
        {
            var Q0;
            Q0=qSketchRegion(id+"F17",true);
            extrude(context, id + "F18", {"entities" : qUnion([Q0]), "depth" : 4 * mm});
        }
        {
            var Q0;
            Q0=qCreatedBy(makeId("Front.planeOp"),FACE);
            var sketch = newSketch(context, id + "F19", { "sketchPlane" : qUnion([Q0])});
            skLineSegment(sketch, "E300", {"start": v(-63, 37) * mm, "end": v(-63, 25) * mm});
            skLineSegment(sketch, "E301", {"start": v(-63, 25) * mm, "end": v(-59, 25) * mm});
            skLineSegment(sketch, "E302", {"start": v(-59, 25) * mm, "end": v(-59, 16) * mm});
            skLineSegment(sketch, "E303", {"start": v(-59, 16) * mm, "end": v(-32.5, 16) * mm});
            skLineSegment(sketch, "E304", {"start": v(-32.5, 16) * mm, "end": v(-32.5, 12) * mm});
            skLineSegment(sketch, "E305", {"start": v(-32.5, 12) * mm, "end": v(-6, 12) * mm});
            skLineSegment(sketch, "E306", {"start": v(-6, 12) * mm, "end": v(-6, 16) * mm});
            skLineSegment(sketch, "E307", {"start": v(-6, 16) * mm, "end": v(20.5, 16) * mm});
            skLineSegment(sketch, "E308", {"start": v(20.5, 16) * mm, "end": v(20.5, 25) * mm});
            skLineSegment(sketch, "E309", {"start": v(20.5, 25) * mm, "end": v(24.5, 25) * mm});
            skLineSegment(sketch, "E310", {"start": v(24.5, 25) * mm, "end": v(24.5, 37) * mm});
            skLineSegment(sketch, "E311", {"start": v(24.5, 37) * mm, "end": v(20.5, 37) * mm});
            skLineSegment(sketch, "E312", {"start": v(20.5, 37) * mm, "end": v(20.5, 46) * mm});
            skLineSegment(sketch, "E313", {"start": v(20.5, 46) * mm, "end": v(-59, 46) * mm});
            skLineSegment(sketch, "E314", {"start": v(-59, 46) * mm, "end": v(-59, 37) * mm});
            skLineSegment(sketch, "E315", {"start": v(-59, 37) * mm, "end": v(-63, 37) * mm});
            skSolve(sketch);
        }
        {
            var Q0;
            Q0=qSketchRegion(id+"F19",true);
            extrude(context, id + "F20", {"entities" : qUnion([Q0]), "depth" : 4 * mm});
        }
        {
            var Q0;
            Q0=qCreatedBy(makeId("Front.planeOp"),FACE);
            var sketch = newSketch(context, id + "F21", { "sketchPlane" : qUnion([Q0])});
            skLineSegment(sketch, "E316.bottom", {"start": v(20.5, 46) * mm, "end": v(-59, 46) * mm});
            skLineSegment(sketch, "E316.top", {"start": v(20.5, 16) * mm, "end": v(-59, 16) * mm});
            skLineSegment(sketch, "E316.left", {"start": v(20.5, 46) * mm, "end": v(20.5, 16) * mm});
            skLineSegment(sketch, "E316.right", {"start": v(-59, 46) * mm, "end": v(-59, 16) * mm});
            skLineSegment(sketch, "E317.bottom", {"start": v(24.5, 37) * mm, "end": v(20.5, 37) * mm});
            skLineSegment(sketch, "E317.top", {"start": v(24.5, 25) * mm, "end": v(20.5, 25) * mm});
            skLineSegment(sketch, "E317.left", {"start": v(24.5, 37) * mm, "end": v(24.5, 25) * mm});
            skLineSegment(sketch, "E317.right", {"start": v(20.5, 37) * mm, "end": v(20.5, 25) * mm});
            skLineSegment(sketch, "E318.bottom", {"start": v(-63, 37) * mm, "end": v(-59, 37) * mm});
            skLineSegment(sketch, "E318.top", {"start": v(-63, 25) * mm, "end": v(-59, 25) * mm});
            skLineSegment(sketch, "E318.left", {"start": v(-63, 37) * mm, "end": v(-63, 25) * mm});
            skLineSegment(sketch, "E318.right", {"start": v(-59, 37) * mm, "end": v(-59, 25) * mm});
            skLineSegment(sketch, "E319.bottom", {"start": v(12.4, 12) * mm, "end": v(-0.63, 12) * mm});
            skLineSegment(sketch, "E319.top", {"start": v(12.4, 16) * mm, "end": v(-0.63, 16) * mm});
            skLineSegment(sketch, "E319.left", {"start": v(12.4, 12) * mm, "end": v(12.4, 16) * mm});
            skLineSegment(sketch, "E319.right", {"start": v(-0.63, 12) * mm, "end": v(-0.63, 16) * mm});
            skLineSegment(sketch, "E320.bottom", {"start": v(-12.73, 16) * mm, "end": v(-25.77, 16) * mm});
            skLineSegment(sketch, "E320.top", {"start": v(-12.73, 12) * mm, "end": v(-25.77, 12) * mm});
            skLineSegment(sketch, "E320.left", {"start": v(-12.73, 16) * mm, "end": v(-12.73, 12) * mm});
            skLineSegment(sketch, "E320.right", {"start": v(-25.77, 16) * mm, "end": v(-25.77, 12) * mm});
            skLineSegment(sketch, "E321.bottom", {"start": v(-37.87, 12) * mm, "end": v(-50.9, 12) * mm});
            skLineSegment(sketch, "E321.top", {"start": v(-37.87, 16) * mm, "end": v(-50.9, 16) * mm});
            skLineSegment(sketch, "E321.left", {"start": v(-37.87, 12) * mm, "end": v(-37.87, 16) * mm});
            skLineSegment(sketch, "E321.right", {"start": v(-50.9, 12) * mm, "end": v(-50.9, 16) * mm});
            skSolve(sketch);
        }
        {
            var Q0;
            Q0=qSketchRegion(id+"F21",true);
            extrude(context, id + "F22", {"entities" : qUnion([Q0]), "oppositeDirection" : true, "depth" : 4 * mm});
        }
        {
            var Q0;
            Q0=qCreatedBy(makeId("Right.planeOp"),FACE);
            var sketch = newSketch(context, id + "F23", { "sketchPlane" : qUnion([Q0])});
            skLineSegment(sketch, "E322.bottom", {"start": v(150.5, 46) * mm, "end": v(75.87, 46) * mm});
            skLineSegment(sketch, "E322.top", {"start": v(150.5, 16) * mm, "end": v(47, 16) * mm});
            skLineSegment(sketch, "E322.left", {"start": v(150.5, 46) * mm, "end": v(150.5, 37) * mm});
            skLineSegment(sketch, "E322.right", {"start": v(47, 46) * mm, "end": v(47, 37) * mm});
            skLineSegment(sketch, "E323", {"start": v(47, 37) * mm, "end": v(51, 37) * mm});
            skLineSegment(sketch, "E324", {"start": v(51, 37) * mm, "end": v(51, 25) * mm});
            skLineSegment(sketch, "E325", {"start": v(51, 25) * mm, "end": v(47, 25) * mm});
            skLineSegment(sketch, "E326", {"start": v(150.5, 25) * mm, "end": v(146.5, 25) * mm});
            skLineSegment(sketch, "E327", {"start": v(146.5, 25) * mm, "end": v(146.5, 37) * mm});
            skLineSegment(sketch, "E328", {"start": v(146.5, 37) * mm, "end": v(150.5, 37) * mm});
            skLineSegment(sketch, "E329.trimOffspring", {"start": v(150.5, 25) * mm, "end": v(150.5, 16) * mm});
            skLineSegment(sketch, "E330.trimOffspring", {"start": v(47, 25) * mm, "end": v(47, 16) * mm});
            skLineSegment(sketch, "E331.left", {"start": v(137.5, 16) * mm, "end": v(137.5, 12) * mm});
            skLineSegment(sketch, "E331.right", {"start": v(127.87, 16) * mm, "end": v(127.87, 12) * mm});
            skLineSegment(sketch, "E332.bottom", {"start": v(114.87, 16) * mm, "end": v(105.25, 16) * mm});
            skLineSegment(sketch, "E332.left", {"start": v(114.87, 16) * mm, "end": v(114.87, 12) * mm});
            skLineSegment(sketch, "E332.right", {"start": v(105.25, 16) * mm, "end": v(105.25, 12) * mm});
            skLineSegment(sketch, "E333.bottom", {"start": v(92.25, 16) * mm, "end": v(82.62, 16) * mm});
            skLineSegment(sketch, "E333.left", {"start": v(92.25, 16) * mm, "end": v(92.25, 12) * mm});
            skLineSegment(sketch, "E333.right", {"start": v(82.62, 16) * mm, "end": v(82.62, 12) * mm});
            skLineSegment(sketch, "E334.bottom", {"start": v(69.62, 16) * mm, "end": v(60, 16) * mm});
            skLineSegment(sketch, "E334.left", {"start": v(69.62, 16) * mm, "end": v(69.62, 12) * mm});
            skLineSegment(sketch, "E334.right", {"start": v(60, 16) * mm, "end": v(60, 12) * mm});
            skLineSegment(sketch, "E335.bottom", {"start": v(125.62, 37) * mm, "end": v(121.62, 37) * mm});
            skLineSegment(sketch, "E335.top", {"start": v(125.62, 25) * mm, "end": v(121.62, 25) * mm});
            skLineSegment(sketch, "E335.left", {"start": v(125.62, 37) * mm, "end": v(125.62, 25) * mm});
            skLineSegment(sketch, "E335.right", {"start": v(121.62, 37) * mm, "end": v(121.62, 25) * mm});
            skLineSegment(sketch, "E336.bottom", {"start": v(100.75, 37) * mm, "end": v(96.75, 37) * mm});
            skLineSegment(sketch, "E336.top", {"start": v(100.75, 25) * mm, "end": v(96.75, 25) * mm});
            skLineSegment(sketch, "E336.left", {"start": v(100.75, 37) * mm, "end": v(100.75, 25) * mm});
            skLineSegment(sketch, "E336.right", {"start": v(96.75, 37) * mm, "end": v(96.75, 25) * mm});
            skLineSegment(sketch, "E337", {"start": v(71.87, 46) * mm, "end": v(71.87, 37) * mm});
            skLineSegment(sketch, "E338", {"start": v(71.87, 37) * mm, "end": v(75.87, 37) * mm});
            skLineSegment(sketch, "E339", {"start": v(75.87, 37) * mm, "end": v(75.87, 46) * mm});
            skLineSegment(sketch, "E340.trimOffspring", {"start": v(71.87, 46) * mm, "end": v(47, 46) * mm});
            skLineSegment(sketch, "E341", {"start": v(60, 12) * mm, "end": v(69.62, 12) * mm});
            skLineSegment(sketch, "E342", {"start": v(82.62, 12) * mm, "end": v(92.25, 12) * mm});
            skLineSegment(sketch, "E343", {"start": v(105.25, 12) * mm, "end": v(114.87, 12) * mm});
            skLineSegment(sketch, "E344", {"start": v(127.87, 12) * mm, "end": v(137.5, 12) * mm});
            skSolve(sketch);
        }
        {
            var Q0;
            Q0=qSketchRegion(id+"F23",true);
            extrude(context, id + "F24", {"entities" : qUnion([Q0]), "depth" : 4 * mm});
        }
        {
            var Q0;
            Q0=qCreatedBy(makeId("Front.planeOp"),FACE);
            var sketch = newSketch(context, id + "F25", { "sketchPlane" : qUnion([Q0])});
            skLineSegment(sketch, "E345", {"start": v(-63, 46) * mm, "end": v(-63, 37) * mm});
            skLineSegment(sketch, "E346", {"start": v(-63, 37) * mm, "end": v(-59, 37) * mm});
            skLineSegment(sketch, "E347", {"start": v(-59, 37) * mm, "end": v(-59, 16) * mm});
            skLineSegment(sketch, "E348", {"start": v(-59, 16) * mm, "end": v(20.5, 16) * mm});
            skLineSegment(sketch, "E349", {"start": v(20.5, 16) * mm, "end": v(20.5, 37) * mm});
            skLineSegment(sketch, "E350", {"start": v(20.5, 37) * mm, "end": v(24.5, 37) * mm});
            skLineSegment(sketch, "E351", {"start": v(24.5, 37) * mm, "end": v(24.5, 46) * mm});
            skLineSegment(sketch, "E352", {"start": v(24.5, 46) * mm, "end": v(-63, 46) * mm});
            skSolve(sketch);
        }
        {
            var Q0;
            Q0=qSketchRegion(id+"F25",true);
            extrude(context, id + "F26", {"entities" : qUnion([Q0]), "depth" : 4 * mm});
        }
        {
            var Q0;
            Q0=qCreatedBy(makeId("Right.planeOp"),FACE);
            var sketch = newSketch(context, id + "F27", { "sketchPlane" : qUnion([Q0])});
            skLineSegment(sketch, "E353", {"start": v(14, 46) * mm, "end": v(-57, 46) * mm});
            skLineSegment(sketch, "E354", {"start": v(-57, 46) * mm, "end": v(-57, 34) * mm});
            skLineSegment(sketch, "E355", {"start": v(-57, 34) * mm, "end": v(-151, 34) * mm});
            skLineSegment(sketch, "E356", {"start": v(-151, 34) * mm, "end": v(-151, 4) * mm});
            skLineSegment(sketch, "E357", {"start": v(-151, 4) * mm, "end": v(-123.5, 4) * mm});
            skLineSegment(sketch, "E358", {"start": v(14, 4) * mm, "end": v(14, 46) * mm});
            skLineSegment(sketch, "E359.bottom", {"start": v(-123.5, 19) * mm, "end": v(-119.5, 19) * mm});
            skLineSegment(sketch, "E359.left", {"start": v(-123.5, 19) * mm, "end": v(-123.5, 4) * mm});
            skLineSegment(sketch, "E359.right", {"start": v(-119.5, 19) * mm, "end": v(-119.5, 4) * mm});
            skLineSegment(sketch, "E360.bottom", {"start": v(-86, 19) * mm, "end": v(-82, 19) * mm});
            skLineSegment(sketch, "E360.left", {"start": v(-86, 19) * mm, "end": v(-86, 4) * mm});
            skLineSegment(sketch, "E360.right", {"start": v(-82, 19) * mm, "end": v(-82, 4) * mm});
            skLineSegment(sketch, "E361.bottom", {"start": v(-48.5, 25) * mm, "end": v(-44.5, 25) * mm});
            skLineSegment(sketch, "E361.left", {"start": v(-48.5, 25) * mm, "end": v(-48.5, 4) * mm});
            skLineSegment(sketch, "E361.right", {"start": v(-44.5, 25) * mm, "end": v(-44.5, 4) * mm});
            skLineSegment(sketch, "E362", {"start": v(-151, 19) * mm, "end": v(-123.5, 19) * mm, "construction": true});
            skLineSegment(sketch, "E363", {"start": v(-119.5, 19) * mm, "end": v(-86, 19) * mm, "construction": true});
            skLineSegment(sketch, "E364", {"start": v(-82, 19) * mm, "end": v(-48.5, 19) * mm, "construction": true});
            skLineSegment(sketch, "E365", {"start": v(-82, 19) * mm, "end": v(-82, 34) * mm, "construction": true});
            skLineSegment(sketch, "E366", {"start": v(-44.5, 25) * mm, "end": v(-44.5, 46) * mm, "construction": true});
            skLineSegment(sketch, "E367.trimOffspring", {"start": v(-119.5, 4) * mm, "end": v(-86, 4) * mm});
            skLineSegment(sketch, "E368.trimOffspring", {"start": v(-82, 4) * mm, "end": v(-48.5, 4) * mm});
            skLineSegment(sketch, "E369.trimOffspring", {"start": v(-44.5, 4) * mm, "end": v(14, 4) * mm});
            skSolve(sketch);
        }
        {
            var Q0;
            Q0=qSketchRegion(id+"F27",true);
            extrude(context, id + "F28", {"entities" : qUnion([Q0]), "oppositeDirection" : true, "depth" : (getVariable(context, 'thickness')) * mm});
        }
        {
            var Q0;
            Q0=qCreatedBy(makeId("Front.planeOp"),FACE);
            var sketch = newSketch(context, id + "F29", { "sketchPlane" : qUnion([Q0])});
            skLineSegment(sketch, "E370", {"start": v(-67, 46) * mm, "end": v(-55, 46) * mm});
            skLineSegment(sketch, "E371", {"start": v(-51, 42) * mm, "end": v(-51, 34) * mm});
            skLineSegment(sketch, "E372", {"start": v(-51, 34) * mm, "end": v(-21, 34) * mm});
            skLineSegment(sketch, "E373", {"start": v(13, 34) * mm, "end": v(13, 42) * mm});
            skLineSegment(sketch, "E374", {"start": v(17, 46) * mm, "end": v(29, 46) * mm});
            skLineSegment(sketch, "E375", {"start": v(29, 46) * mm, "end": v(29, 34) * mm});
            skLineSegment(sketch, "E376", {"start": v(25, 34) * mm, "end": v(25, 4) * mm});
            skLineSegment(sketch, "E377", {"start": v(25, 4) * mm, "end": v(-63, 4) * mm});
            skLineSegment(sketch, "E378", {"start": v(-63, 4) * mm, "end": v(-63, 34) * mm});
            skLineSegment(sketch, "E379", {"start": v(-63, 34) * mm, "end": v(-67, 34) * mm});
            skLineSegment(sketch, "E380", {"start": v(-67, 34) * mm, "end": v(-67, 46) * mm});
            skLineSegment(sketch, "E381", {"start": v(29, 34) * mm, "end": v(25, 34) * mm});
            skLineSegment(sketch, "E382", {"start": v(-63, 34) * mm, "end": v(-51, 34) * mm, "construction": true});
            skLineSegment(sketch, "E383", {"start": v(25, 34) * mm, "end": v(13, 34) * mm, "construction": true});
            skLineSegment(sketch, "E384.top", {"start": v(-21, 19) * mm, "end": v(-17, 19) * mm});
            skLineSegment(sketch, "E384.left", {"start": v(-21, 34) * mm, "end": v(-21, 19) * mm});
            skLineSegment(sketch, "E384.right", {"start": v(-17, 34) * mm, "end": v(-17, 19) * mm});
            skLineSegment(sketch, "E385.trimOffspring", {"start": v(-17, 34) * mm, "end": v(13, 34) * mm});
            skPoint(sketch, "E386.visualSharp", {"position": v(-51, 46) * mm});
            skArc(sketch, "E386.filletArc", {"start": v(-51, 42) * mm, "mid": v(-52.17, 44.83) * mm, "end": v(-55, 46) * mm});
            skPoint(sketch, "E387.visualSharp", {"position": v(13, 46) * mm});
            skArc(sketch, "E387.filletArc", {"start": v(17, 46) * mm, "mid": v(14.17, 44.83) * mm, "end": v(13, 42) * mm});
            skSolve(sketch);
        }
        {
            var Q0;
            Q0=qSketchRegion(id+"F29",true);
            extrude(context, id + "F30", {"entities" : qUnion([Q0]), "depth" : (getVariable(context, 'thickness')) * mm});
        }
        {
            var Q0;
            Q0=qCreatedBy(makeId("Front.planeOp"),FACE);
            var sketch = newSketch(context, id + "F31", { "sketchPlane" : qUnion([Q0])});
            skLineSegment(sketch, "E388", {"start": v(-67, 46) * mm, "end": v(-67, 34) * mm});
            skLineSegment(sketch, "E389", {"start": v(-67, 34) * mm, "end": v(-63, 34) * mm});
            skLineSegment(sketch, "E390", {"start": v(-63, 34) * mm, "end": v(-63, 4) * mm});
            skLineSegment(sketch, "E391", {"start": v(-63, 4) * mm, "end": v(25, 4) * mm});
            skLineSegment(sketch, "E392", {"start": v(25, 4) * mm, "end": v(25, 34) * mm});
            skLineSegment(sketch, "E393", {"start": v(25, 34) * mm, "end": v(29, 34) * mm});
            skLineSegment(sketch, "E394", {"start": v(29, 34) * mm, "end": v(29, 46) * mm});
            skLineSegment(sketch, "E395", {"start": v(29, 46) * mm, "end": v(-17, 46) * mm});
            skLineSegment(sketch, "E396.top", {"start": v(-21, 25) * mm, "end": v(-17, 25) * mm});
            skLineSegment(sketch, "E396.left", {"start": v(-21, 46) * mm, "end": v(-21, 25) * mm});
            skLineSegment(sketch, "E396.right", {"start": v(-17, 46) * mm, "end": v(-17, 25) * mm});
            skLineSegment(sketch, "E397.trimOffspring", {"start": v(-21, 46) * mm, "end": v(-67, 46) * mm});
            skSolve(sketch);
        }
        {
            var Q0;
            Q0=qSketchRegion(id+"F31",true);
            extrude(context, id + "F32", {"entities" : qUnion([Q0]), "oppositeDirection" : true, "depth" : (getVariable(context, 'thickness')) * mm});
        }
        {
            var Q0;
            Q0=qCreatedBy(makeId("Front.planeOp"),FACE);
            var sketch = newSketch(context, id + "F33", { "sketchPlane" : qUnion([Q0])});
            skLineSegment(sketch, "E398", {"start": v(25, 46) * mm, "end": v(25, 34) * mm});
            skLineSegment(sketch, "E399", {"start": v(25, 34) * mm, "end": v(29, 34) * mm});
            skLineSegment(sketch, "E400", {"start": v(29, 34) * mm, "end": v(29, 4) * mm});
            skLineSegment(sketch, "E401", {"start": v(29, 4) * mm, "end": v(106, 4) * mm});
            skLineSegment(sketch, "E402", {"start": v(106, 4) * mm, "end": v(106, 34) * mm});
            skLineSegment(sketch, "E403", {"start": v(106, 34) * mm, "end": v(110, 34) * mm});
            skLineSegment(sketch, "E404", {"start": v(110, 34) * mm, "end": v(110, 46) * mm});
            skLineSegment(sketch, "E405", {"start": v(110, 46) * mm, "end": v(94.2, 46) * mm});
            skLineSegment(sketch, "E406", {"start": v(25, 46) * mm, "end": v(40.8, 46) * mm});
            skArc(sketch, "E407", {"start": v(44.75, 42.6) * mm, "mid": v(67.5, 23) * mm, "end": v(90.25, 42.6) * mm});
            skPoint(sketch, "E408.visualSharp", {"position": v(44.5, 46) * mm});
            skArc(sketch, "E408.filletArc", {"start": v(44.75, 42.6) * mm, "mid": v(43.4, 45.03) * mm, "end": v(40.8, 46) * mm});
            skPoint(sketch, "E409.visualSharp", {"position": v(90.5, 46) * mm});
            skArc(sketch, "E409.filletArc", {"start": v(94.2, 46) * mm, "mid": v(91.6, 45.03) * mm, "end": v(90.25, 42.6) * mm});
            skSolve(sketch);
        }
        {
            var Q0;
            Q0=qSketchRegion(id+"F33",true);
            extrude(context, id + "F34", {"entities" : qUnion([Q0]), "depth" : (getVariable(context, 'thickness')) * mm});
        }
        {
            var Q0;
            Q0=qCreatedBy(makeId("Front.planeOp"),FACE);
            var sketch = newSketch(context, id + "F35", { "sketchPlane" : qUnion([Q0])});
            skLineSegment(sketch, "E410", {"start": v(-110, 46) * mm, "end": v(-110, 34) * mm});
            skLineSegment(sketch, "E411", {"start": v(-110, 34) * mm, "end": v(-106, 34) * mm});
            skLineSegment(sketch, "E412", {"start": v(-106, 34) * mm, "end": v(-106, 4) * mm});
            skLineSegment(sketch, "E413", {"start": v(-106, 4) * mm, "end": v(-67, 4) * mm});
            skLineSegment(sketch, "E414", {"start": v(-67, 4) * mm, "end": v(-67, 34) * mm});
            skLineSegment(sketch, "E415", {"start": v(-67, 34) * mm, "end": v(-63, 34) * mm});
            skLineSegment(sketch, "E416", {"start": v(-63, 34) * mm, "end": v(-63, 46) * mm});
            skLineSegment(sketch, "E417", {"start": v(-63, 46) * mm, "end": v(-71.5, 46) * mm});
            skLineSegment(sketch, "E418", {"start": v(-75.5, 42) * mm, "end": v(-75.5, 34) * mm});
            skLineSegment(sketch, "E419", {"start": v(-110, 46) * mm, "end": v(-101.5, 46) * mm});
            skLineSegment(sketch, "E420", {"start": v(-97.5, 42) * mm, "end": v(-97.5, 34) * mm});
            skArc(sketch, "E421", {"start": v(-97.5, 34) * mm, "mid": v(-86.5, 23) * mm, "end": v(-75.5, 34) * mm});
            skLineSegment(sketch, "E422", {"start": v(-75.5, 34) * mm, "end": v(-97.5, 34) * mm, "construction": true});
            skPoint(sketch, "E423.visualSharp", {"position": v(-75.5, 46) * mm});
            skArc(sketch, "E423.filletArc", {"start": v(-71.5, 46) * mm, "mid": v(-74.33, 44.83) * mm, "end": v(-75.5, 42) * mm});
            skPoint(sketch, "E424.visualSharp", {"position": v(-97.5, 46) * mm});
            skArc(sketch, "E424.filletArc", {"start": v(-97.5, 42) * mm, "mid": v(-98.67, 44.83) * mm, "end": v(-101.5, 46) * mm});
            skSolve(sketch);
        }
        {
            var Q0;
            Q0=qSketchRegion(id+"F35",true);
            extrude(context, id + "F36", {"entities" : qUnion([Q0]), "depth" : (getVariable(context, 'thickness')) * mm});
        }
    });
